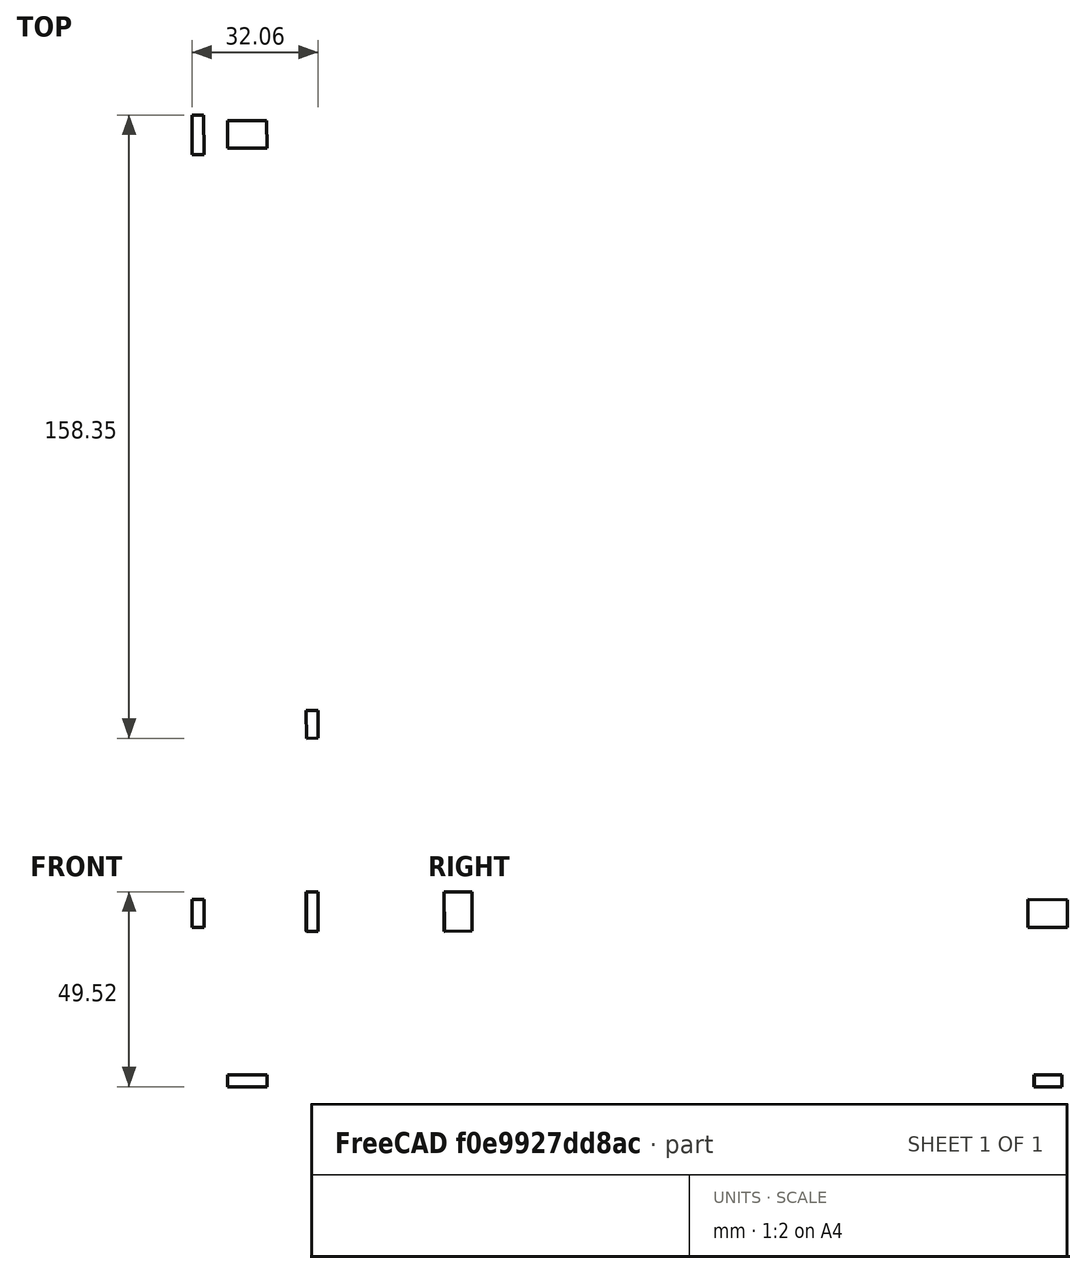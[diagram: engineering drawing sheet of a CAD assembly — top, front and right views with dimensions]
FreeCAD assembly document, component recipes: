
FREECAD ASSEMBLY — COMPONENT RECIPES ("3axis_robot_rotation")

This assembly document has 14 components, labeled P0..P13 below (a component is one placed body or linked part). 11 of them carry a construction recipe — the FreeCAD feature program that regenerates the part from scratch, quoted from this document or its linked companion documents; the rest are supplied as boundary geometry only. No exploded tour is included for this assembly.
COMPONENT P0 — recipe-attached ("arm0", a linked part whose construction recipe lives in a companion FreeCAD document of the same project; that document's serialized recipe follows).
Construction recipe (the companion document, serialized — sketch geometry with constraints, then the solid features built on it; lengths are millimeters unless a unit is written):

FCSTD DOCUMENT  (FreeCAD 2024.1R35694 (Git))
Label: arm0
License: All rights reserved
LicenseURL: https://en.wikipedia.org/wiki/All_rights_reserved
objects: Sketcher::SketchObject×11, PartDesign::Pad×6, PartDesign::Hole×3, PartDesign::Body×2, PartDesign::Pocket×2, PartDesign::Fillet×1, App::Part×1
note: 37 computed .brp shape members not serialized (recipe doc carries the construction recipe); baked Part::Feature solids carry a one-line shape summary decoded from their .brp

FEATURE [Sketcher::SketchObject] Sketch
  FullyConstrained = true
  MapMode = 5
  Support = -> [XY_Plane001]
  sketch-geometry (5):
    g0: Circle CenterX=0 CenterY=0 CenterZ=0 NormalX=0 NormalY=0 NormalZ=1 AngleXU=0 Radius=2.5
    g1: ArcOfCircle CenterX=0 CenterY=0 CenterZ=0 NormalX=0 NormalY=0 NormalZ=1 AngleXU=0 Radius=7.5 StartAngle=1.5708 EndAngle=4.71239
    g2: LineSegment StartX=-1.2e-15 StartY=7.5 StartZ=0 EndX=15 EndY=7.5 EndZ=0
    g3: LineSegment StartX=15 StartY=7.5 StartZ=0 EndX=15 EndY=-7.5 EndZ=0
    g4: LineSegment StartX=15 StartY=-7.5 StartZ=0 EndX=1.8e-15 EndY=-7.5 EndZ=0
  constraints (12):
    c: Coincident(g0,g-1)
    c: Coincident(g1,g0)
    c: Diameter(g0) = 5
    c: Diameter(g1) = 15
    c: Horizontal(g2)
    c: Coincident(g2,g3)
    c: Vertical(g3)
    c: Coincident(g3,g4)
    c: Horizontal(g4)
    c: Tangent(g1,g4) = 1.5708
    c: Tangent(g1,g2) = 1.5708
    c: DistanceX(g2,g2) = 15
FEATURE [PartDesign::Pad] Pad
  Direction = (0,0,1)
  Length = 20
  Length2 = 10
  Profile = -> Sketch
  ReferenceAxis = -> Sketch [N_Axis]
  Refine = true
  Type = 0
FEATURE [Sketcher::SketchObject] Sketch001
  ExternalGeometry = -> [Pad]
  FullyConstrained = true
  MapMode = 5
  Placement = pos=(15,0,0) rot=(0.57735,0.57735,0.57735;2.0944rad)
  Support = -> [Pad]
  sketch-geometry (8):
    g0: LineSegment StartX=-7.5 StartY=0 StartZ=0 EndX=-21 EndY=43 EndZ=0
    g1: LineSegment StartX=-21 StartY=43 StartZ=0 EndX=-21 EndY=85 EndZ=0
    g2: LineSegment StartX=-21 StartY=85 StartZ=0 EndX=21 EndY=85 EndZ=0
    g3: LineSegment StartX=21 StartY=85 StartZ=0 EndX=21 EndY=43 EndZ=0
    g4: LineSegment StartX=21 StartY=43 StartZ=0 EndX=7.5 EndY=0 EndZ=0
    g5: LineSegment StartX=7.5 StartY=0 StartZ=0 EndX=-7.5 EndY=0 EndZ=0
    g6: GeomPoint X=5.2e-15 Y=64 Z=0
    g7: Circle CenterX=5.2e-15 CenterY=64 CenterZ=0 NormalX=0 NormalY=0 NormalZ=1 AngleXU=0 Radius=11.25
  constraints (18):
    c: PointOnObject(g0,g-1)
    c: Coincident(g0,g1)
    c: Vertical(g1)
    c: Coincident(g1,g2)
    c: Coincident(g2,g3)
    c: Coincident(g3,g4)
    c: Coincident(g4,g5)
    c: Coincident(g5,g0)
    c: Symmetric(g0,g3,g-2)
    c: Symmetric(g1,g2,g-2)
    c: DistanceX(g2,g2) = 42
    c: DistanceY(g3,g3) = 42
    c: Symmetric(g0,g4,g-2)
    c: DistanceX(g5,g5) = 15
    c: Symmetric(g1,g3,g6)
    c: Coincident(g7,g6)
    c: Diameter(g7) = 22.5
    c: DistanceY(g-1,g3) = 43
FEATURE [PartDesign::Pad] Pad001
  BaseFeature = -> Pad
  Direction = (1,0,0)
  Length = 4
  Length2 = 10
  Profile = -> Sketch001
  ReferenceAxis = -> Sketch001 [N_Axis]
  Refine = true
  Reversed = true
  Type = 0
FEATURE [Sketcher::SketchObject] Sketch003
  ExternalGeometry = -> [Pad001]
  FullyConstrained = true
  MapMode = 5
  Placement = pos=(11,0,0) rot=(0.57735,-0.57735,-0.57735;2.0944rad)
  Support = -> [Pad001]
  sketch-geometry (5):
    g0: Circle CenterX=15.5 CenterY=79.5 CenterZ=0 NormalX=0 NormalY=0 NormalZ=1 AngleXU=0 Radius=1.5
    g1: LineSegment StartX=-5.2e-15 StartY=64 StartZ=0 EndX=11.25 EndY=64 EndZ=0
    g2: Circle CenterX=-15.5 CenterY=79.5 CenterZ=0 NormalX=0 NormalY=0 NormalZ=1 AngleXU=0 Radius=1.5
    g3: Circle CenterX=15.5 CenterY=48.5 CenterZ=0 NormalX=0 NormalY=0 NormalZ=1 AngleXU=0 Radius=1.5
    g4: Circle CenterX=-15.5 CenterY=48.5 CenterZ=0 NormalX=0 NormalY=0 NormalZ=1 AngleXU=0 Radius=1.5
  constraints (12):
    c: DistanceY(g-3,g0) = 15.5
    c: DistanceX(g-3,g0) = 15.5
    c: Diameter(g0) = 3
    c: Coincident(g1,g-3)
    c: Horizontal(g1)
    c: PointOnObject(g1,g-3)
    c: Diameter(g2) = 3
    c: Diameter(g3) = 3
    c: Diameter(g4) = 3
    c: Symmetric(g2,g0,g-2)
    c: Symmetric(g4,g3,g-2)
    c: Symmetric(g3,g0,g1)
FEATURE [PartDesign::Hole] Hole
  BaseFeature = -> Pad001
  CustomThreadClearance = 0
  Depth = 25
  DepthType = 0
  Diameter = 3.4
  DrillForDepth = false
  DrillPoint = 1
  DrillPointAngle = 118
  HoleCutCountersinkAngle = 90
  HoleCutCustomValues = false
  HoleCutDepth = 2
  HoleCutDiameter = 6.1
  HoleCutType = 1
  ModelThread = false
  Profile = -> Sketch003
  Refine = true
  Tapered = false
  TaperedAngle = 90
  ThreadClass = 0
  ThreadDepth = 25
  ThreadDepthType = 0
  ThreadDirection = 0
  ThreadFit = 0
  ThreadSize = 9
  ThreadType = 1
  Threaded = false
  UseCustomThreadClearance = false
FEATURE [Sketcher::SketchObject] Sketch004
  ExternalGeometry = -> [Hole]
  FullyConstrained = true
  MapMode = 5
  Placement = pos=(0,0,20) rot=(0,0,1;0rad)
  Support = -> [Hole]
  sketch-geometry (1):
    g0: Circle CenterX=0 CenterY=0 CenterZ=0 NormalX=0 NormalY=0 NormalZ=1 AngleXU=0 Radius=2.5
  constraints (2):
    c: Coincident(g0,g-3)
    c: Equal(g0,g-3)
FEATURE [PartDesign::Pad] Pad002
  BaseFeature = -> Hole
  Direction = (0,0,1)
  Length = 2
  Length2 = 10
  Profile = -> Sketch004
  ReferenceAxis = -> Sketch004 [N_Axis]
  Refine = true
  Reversed = true
  Type = 0
FEATURE [PartDesign::Body] Body  label="arm0-skel"
  Group = -> [Sketch,Pad,Sketch001,Pad001,Sketch003,Hole,Sketch004,Pad002]
  Origin = -> Origin001
  Tip = -> Pad002
FEATURE [Sketcher::SketchObject] Sketch008
  FullyConstrained = true
  MapMode = 5
  Support = -> [XY_Plane002]
  sketch-geometry (5):
    g0: Circle CenterX=0 CenterY=0 CenterZ=0 NormalX=0 NormalY=0 NormalZ=1 AngleXU=0 Radius=2.5
    g1: ArcOfCircle CenterX=0 CenterY=0 CenterZ=0 NormalX=0 NormalY=0 NormalZ=1 AngleXU=0 Radius=7.5 StartAngle=1.5708 EndAngle=4.71239
    g2: LineSegment StartX=-1.2e-15 StartY=7.5 StartZ=0 EndX=15 EndY=7.5 EndZ=0
    g3: LineSegment StartX=15 StartY=7.5 StartZ=0 EndX=15 EndY=-7.5 EndZ=0
    g4: LineSegment StartX=15 StartY=-7.5 StartZ=0 EndX=1.8e-15 EndY=-7.5 EndZ=0
  constraints (12):
    c: Coincident(g0,g-1)
    c: Coincident(g1,g0)
    c: Diameter(g0) = 5
    c: Diameter(g1) = 15
    c: Horizontal(g2)
    c: Coincident(g2,g3)
    c: Vertical(g3)
    c: Coincident(g3,g4)
    c: Horizontal(g4)
    c: Tangent(g1,g4) = 1.5708
    c: Tangent(g1,g2) = 1.5708
    c: DistanceX(g2,g2) = 15
FEATURE [PartDesign::Pad] Pad003
  Direction = (0,0,1)
  Length = 20
  Length2 = 10
  Profile = -> Sketch008
  ReferenceAxis = -> Sketch008 [N_Axis]
  Refine = true
  Type = 0
FEATURE [Sketcher::SketchObject] Sketch009
  ExternalGeometry = -> [Pad003]
  FullyConstrained = true
  MapMode = 5
  Placement = pos=(15,0,0) rot=(0.57735,0.57735,0.57735;2.0944rad)
  Support = -> [Pad003]
  sketch-geometry (8):
    g0: LineSegment StartX=-7.5 StartY=0 StartZ=0 EndX=-21 EndY=43 EndZ=0
    g1: LineSegment StartX=-21 StartY=43 StartZ=0 EndX=-21 EndY=85 EndZ=0
    g2: LineSegment StartX=-21 StartY=85 StartZ=0 EndX=21 EndY=85 EndZ=0
    g3: LineSegment StartX=21 StartY=85 StartZ=0 EndX=21 EndY=43 EndZ=0
    g4: LineSegment StartX=21 StartY=43 StartZ=0 EndX=7.5 EndY=0 EndZ=0
    g5: LineSegment StartX=7.5 StartY=0 StartZ=0 EndX=-7.5 EndY=0 EndZ=0
    g6: GeomPoint X=4.8e-15 Y=64 Z=0
    g7: Circle CenterX=4.8e-15 CenterY=64 CenterZ=0 NormalX=0 NormalY=0 NormalZ=1 AngleXU=0 Radius=11.25
  constraints (18):
    c: PointOnObject(g0,g-1)
    c: Coincident(g0,g1)
    c: Vertical(g1)
    c: Coincident(g1,g2)
    c: Coincident(g2,g3)
    c: Coincident(g3,g4)
    c: Coincident(g4,g5)
    c: Coincident(g5,g0)
    c: Symmetric(g0,g3,g-2)
    c: Symmetric(g1,g2,g-2)
    c: DistanceX(g2,g2) = 42
    c: DistanceY(g3,g3) = 42
    c: Symmetric(g0,g4,g-2)
    c: DistanceX(g5,g5) = 15
    c: Symmetric(g1,g3,g6)
    c: Coincident(g7,g6)
    c: Diameter(g7) = 22.5
    c: DistanceY(g-1,g3) = 43
FEATURE [PartDesign::Pad] Pad004
  BaseFeature = -> Pad003
  Direction = (1,0,0)
  Length = 4
  Length2 = 10
  Profile = -> Sketch009
  ReferenceAxis = -> Sketch009 [N_Axis]
  Refine = true
  Reversed = true
  Type = 0
FEATURE [Sketcher::SketchObject] Sketch010
  ExternalGeometry = -> [Pad004]
  FullyConstrained = true
  MapMode = 5
  Placement = pos=(11,0,0) rot=(0.57735,-0.57735,-0.57735;2.0944rad)
  Support = -> [Pad004]
  sketch-geometry (5):
    g0: Circle CenterX=15.5 CenterY=79.5 CenterZ=0 NormalX=0 NormalY=0 NormalZ=1 AngleXU=0 Radius=1.5
    g1: LineSegment StartX=-4.8e-15 StartY=64 StartZ=0 EndX=11.25 EndY=64 EndZ=0
    g2: Circle CenterX=-15.5 CenterY=79.5 CenterZ=0 NormalX=0 NormalY=0 NormalZ=1 AngleXU=0 Radius=1.5
    g3: Circle CenterX=15.5 CenterY=48.5 CenterZ=0 NormalX=0 NormalY=0 NormalZ=1 AngleXU=0 Radius=1.5
    g4: Circle CenterX=-15.5 CenterY=48.5 CenterZ=0 NormalX=0 NormalY=0 NormalZ=1 AngleXU=0 Radius=1.5
  constraints (12):
    c: DistanceY(g-3,g0) = 15.5
    c: DistanceX(g-3,g0) = 15.5
    c: Diameter(g0) = 3
    c: Coincident(g1,g-3)
    c: Horizontal(g1)
    c: PointOnObject(g1,g-3)
    c: Diameter(g2) = 3
    c: Diameter(g3) = 3
    c: Diameter(g4) = 3
    c: Symmetric(g2,g0,g-2)
    c: Symmetric(g4,g3,g-2)
    c: Symmetric(g3,g0,g1)
FEATURE [PartDesign::Hole] Hole002
  BaseFeature = -> Pad004
  CustomThreadClearance = 0
  Depth = 25
  DepthType = 0
  Diameter = 3.4
  DrillForDepth = false
  DrillPoint = 1
  DrillPointAngle = 118
  HoleCutCountersinkAngle = 90
  HoleCutCustomValues = false
  HoleCutDepth = 2
  HoleCutDiameter = 6.1
  HoleCutType = 1
  ModelThread = false
  Profile = -> Sketch010
  Refine = true
  Tapered = false
  TaperedAngle = 90
  ThreadClass = 0
  ThreadDepth = 25
  ThreadDepthType = 0
  ThreadDirection = 0
  ThreadFit = 0
  ThreadSize = 9
  ThreadType = 1
  Threaded = false
  UseCustomThreadClearance = false
FEATURE [Sketcher::SketchObject] Sketch011
  ExternalGeometry = -> [Hole002]
  FullyConstrained = true
  MapMode = 5
  Placement = pos=(0,0,20) rot=(0,0,1;0rad)
  Support = -> [Hole002]
  sketch-geometry (1):
    g0: Circle CenterX=0 CenterY=0 CenterZ=0 NormalX=0 NormalY=0 NormalZ=1 AngleXU=0 Radius=2.5
  constraints (2):
    c: Coincident(g0,g-3)
    c: Equal(g0,g-3)
FEATURE [PartDesign::Pad] Pad005
  BaseFeature = -> Hole002
  Direction = (0,0,1)
  Length = 2
  Length2 = 10
  Profile = -> Sketch011
  ReferenceAxis = -> Sketch011 [N_Axis]
  Refine = true
  Reversed = true
  Type = 0
FEATURE [Sketcher::SketchObject] Sketch012
  FullyConstrained = true
  MapMode = 5
  Placement = pos=(0,0,0) rot=(1,0,0;3.14159rad)
  Support = -> [Pad005]
  sketch-geometry (4):
    g0: LineSegment StartX=0 StartY=1 StartZ=0 EndX=0 EndY=-1 EndZ=0
    g1: LineSegment StartX=0 StartY=-1 StartZ=0 EndX=10 EndY=-1 EndZ=0
    g2: LineSegment StartX=10 StartY=-1 StartZ=0 EndX=10 EndY=1 EndZ=0
    g3: LineSegment StartX=10 StartY=1 StartZ=0 EndX=0 EndY=1 EndZ=0
  constraints (11):
    c: Coincident(g0,g1)
    c: Coincident(g1,g2)
    c: Coincident(g2,g3)
    c: Coincident(g3,g0)
    c: Vertical(g0)
    c: Horizontal(g1)
    c: Horizontal(g3)
    c: PointOnObject(g0,g-2)
    c: Symmetric(g1,g2,g-1)
    c: DistanceY(g2,g2) = 2
    c: DistanceX(g3,g3) = 10
FEATURE [PartDesign::Pocket] Pocket002
  BaseFeature = -> Pad005
  Direction = (0,0,1)
  Length = 5
  Length2 = 5
  Profile = -> Sketch012
  ReferenceAxis = -> Sketch012 [N_Axis]
  Refine = true
  Type = 1
FEATURE [Sketcher::SketchObject] Sketch013
  FullyConstrained = true
  MapMode = 5
  Placement = pos=(0,-7.5,0) rot=(1,0,0;1.5708rad)
  Support = -> [Pocket002]
  sketch-geometry (1):
    g0: Circle CenterX=6 CenterY=10 CenterZ=0 NormalX=0 NormalY=0 NormalZ=1 AngleXU=0 Radius=1.5
  constraints (3):
    c: DistanceY(g-1,g0) = 10
    c: DistanceX(g-1,g0) = 6
    c: Diameter(g0) = 3
FEATURE [PartDesign::Hole] Hole003
  BaseFeature = -> Pocket002
  CustomThreadClearance = 0
  Depth = 25
  DepthType = 0
  Diameter = 4.5
  DrillForDepth = false
  DrillPoint = 1
  DrillPointAngle = 118
  HoleCutCountersinkAngle = 90
  HoleCutCustomValues = false
  HoleCutDepth = 0
  HoleCutDiameter = 6.1
  HoleCutType = 0
  ModelThread = false
  Profile = -> Sketch013
  Refine = true
  Tapered = false
  TaperedAngle = 90
  ThreadClass = 0
  ThreadDepth = 25
  ThreadDepthType = 0
  ThreadDirection = 0
  ThreadFit = 0
  ThreadSize = 11
  ThreadType = 1
  Threaded = false
  UseCustomThreadClearance = false
FEATURE [Sketcher::SketchObject] Sketch014
  ExternalGeometry = -> [Hole003]
  FullyConstrained = true
  MapMode = 5
  Placement = pos=(0,7.5,0) rot=(0,0.707107,0.707107;3.14159rad)
  Support = -> [Hole003]
  sketch-geometry (7):
    g0: LineSegment StartX=-1.95855 StartY=10 StartZ=0 EndX=-3.97927 EndY=13.5 EndZ=0
    g1: LineSegment StartX=-3.97927 StartY=13.5 StartZ=0 EndX=-8.02073 EndY=13.5 EndZ=0
    g2: LineSegment StartX=-8.02073 StartY=13.5 StartZ=0 EndX=-10.0415 EndY=10 EndZ=0
    g3: LineSegment StartX=-10.0415 StartY=10 StartZ=0 EndX=-8.02073 EndY=6.5 EndZ=0
    g4: LineSegment StartX=-8.02073 StartY=6.5 StartZ=0 EndX=-3.97927 EndY=6.5 EndZ=0
    g5: LineSegment StartX=-3.97927 StartY=6.5 StartZ=0 EndX=-1.95855 EndY=10 EndZ=0
    g6: Circle CenterX=-6 CenterY=10 CenterZ=0 NormalX=0 NormalY=0 NormalZ=1 AngleXU=0 Radius=4.04145
  constraints (16):
    c: Coincident(g0,g1)
    c: Coincident(g1,g2)
    c: Coincident(g2,g3)
    c: Coincident(g3,g4)
    c: Coincident(g4,g5)
    c: Coincident(g5,g0)
    c: Equal(g0, g1-g5) x5
    c: PointOnObject(g0,g6)
    c: PointOnObject(g1,g6)
    c: PointOnObject(g2,g6)
    c: PointOnObject(g3,g6)
    c: PointOnObject(g4,g6)
    c: PointOnObject(g5,g6)
    c: Coincident(g6,g-3)
    c: Horizontal(g1)
    c: DistanceY(g4,g0) = 7
FEATURE [PartDesign::Pocket] Pocket003
  BaseFeature = -> Hole003
  Direction = (0,-1,2e-16)
  Length = 4
  Length2 = 5
  Profile = -> Sketch014
  ReferenceAxis = -> Sketch014 [N_Axis]
  Refine = true
  Type = 0
FEATURE [PartDesign::Fillet] Fillet
  Base = -> Pocket003 [Edge77,Edge78,Edge65,Edge54]
  BaseFeature = -> Pocket003
  Radius = 6
  Refine = true
  SupportTransform = false
  UseAllEdges = false
FEATURE [PartDesign::Body] Body001  label="arm0s"
  Group = -> [Sketch008,Pad003,Sketch009,Pad004,Sketch010,Hole002,Sketch011,Pad005,Sketch012,Pocket002,Sketch013,Hole003,Sketch014,Pocket003,Fillet]
  Origin = -> Origin002
  Tip = -> Fillet
FEATURE [App::Part] Part  label="arm0"
  Group = -> [Body,Body001]
  Origin = -> Origin
COMPONENT P1 — recipe-attached ("arm1", a linked part whose construction recipe lives in a companion FreeCAD document of the same project; that document's serialized recipe follows).
Construction recipe (the companion document, serialized — sketch geometry with constraints, then the solid features built on it; lengths are millimeters unless a unit is written):

FCSTD DOCUMENT  (FreeCAD 2024.1R35694 (Git))
Label: arm1
License: All rights reserved
LicenseURL: https://en.wikipedia.org/wiki/All_rights_reserved
objects: Sketcher::SketchObject×17, PartDesign::Pad×11, PartDesign::Chamfer×8, PartDesign::Plane×4, PartDesign::Hole×3, PartDesign::Pocket×3, PartDesign::Body×2, PartDesign::Fillet×1, App::Part×1
note: 75 computed .brp shape members not serialized (recipe doc carries the construction recipe); baked Part::Feature solids carry a one-line shape summary decoded from their .brp

FEATURE [Sketcher::SketchObject] Sketch
  FullyConstrained = true
  MapMode = 5
  Support = -> [XY_Plane001]
  sketch-geometry (5):
    g0: Circle CenterX=0 CenterY=0 CenterZ=0 NormalX=0 NormalY=0 NormalZ=1 AngleXU=0 Radius=2.5
    g1: ArcOfCircle CenterX=0 CenterY=0 CenterZ=0 NormalX=0 NormalY=0 NormalZ=1 AngleXU=0 Radius=7.5 StartAngle=1.5708 EndAngle=4.71239
    g2: LineSegment StartX=-1.2e-15 StartY=7.5 StartZ=0 EndX=15 EndY=7.5 EndZ=0
    g3: LineSegment StartX=15 StartY=7.5 StartZ=0 EndX=15 EndY=-7.5 EndZ=0
    g4: LineSegment StartX=15 StartY=-7.5 StartZ=0 EndX=1.8e-15 EndY=-7.5 EndZ=0
  constraints (12):
    c: Coincident(g0,g-1)
    c: Coincident(g1,g0)
    c: Diameter(g0) = 5
    c: Diameter(g1) = 15
    c: Horizontal(g2)
    c: Coincident(g2,g3)
    c: Vertical(g3)
    c: Coincident(g3,g4)
    c: Horizontal(g4)
    c: Tangent(g1,g4) = 1.5708
    c: Tangent(g1,g2) = 1.5708
    c: DistanceX(g2,g2) = 15
FEATURE [PartDesign::Pad] Pad
  Direction = (0,0,1)
  Length = 20
  Length2 = 10
  Profile = -> Sketch
  ReferenceAxis = -> Sketch [N_Axis]
  Refine = true
  Type = 0
FEATURE [Sketcher::SketchObject] Sketch001
  ExternalGeometry = -> [Pad]
  FullyConstrained = true
  MapMode = 5
  Placement = pos=(15,0,0) rot=(0.57735,0.57735,0.57735;2.0944rad)
  Support = -> [Pad]
  sketch-geometry (8):
    g0: LineSegment StartX=-7.5 StartY=0 StartZ=0 EndX=-21 EndY=11 EndZ=0
    g1: LineSegment StartX=-21 StartY=11 StartZ=0 EndX=-21 EndY=53 EndZ=0
    g2: LineSegment StartX=-21 StartY=53 StartZ=0 EndX=21 EndY=53 EndZ=0
    g3: LineSegment StartX=21 StartY=53 StartZ=0 EndX=21 EndY=11 EndZ=0
    g4: LineSegment StartX=21 StartY=11 StartZ=0 EndX=7.5 EndY=0 EndZ=0
    g5: LineSegment StartX=7.5 StartY=0 StartZ=0 EndX=-7.5 EndY=0 EndZ=0
    g6: GeomPoint X=-1.2e-15 Y=32 Z=0
    g7: Circle CenterX=-1.2e-15 CenterY=32 CenterZ=0 NormalX=0 NormalY=0 NormalZ=1 AngleXU=0 Radius=11.25
  constraints (18):
    c: PointOnObject(g0,g-1)
    c: Coincident(g0,g1)
    c: Vertical(g1)
    c: Coincident(g1,g2)
    c: Coincident(g2,g3)
    c: Coincident(g3,g4)
    c: Coincident(g4,g5)
    c: Coincident(g5,g0)
    c: Symmetric(g0,g3,g-2)
    c: Symmetric(g1,g2,g-2)
    c: DistanceX(g2,g2) = 42
    c: DistanceY(g3,g3) = 42
    c: Symmetric(g0,g4,g-2)
    c: DistanceX(g5,g5) = 15
    c: Symmetric(g1,g3,g6)
    c: Coincident(g7,g6)
    c: Diameter(g7) = 22.5
    c: DistanceY(g-1,g3) = 11
FEATURE [PartDesign::Pad] Pad001
  BaseFeature = -> Pad
  Direction = (1,0,0)
  Length = 4
  Length2 = 10
  Profile = -> Sketch001
  ReferenceAxis = -> Sketch001 [N_Axis]
  Refine = true
  Reversed = true
  Type = 0
FEATURE [Sketcher::SketchObject] Sketch003
  ExternalGeometry = -> [Pad001]
  FullyConstrained = true
  MapMode = 5
  Placement = pos=(11,0,0) rot=(0.57735,-0.57735,-0.57735;2.0944rad)
  Support = -> [Pad001]
  sketch-geometry (5):
    g0: Circle CenterX=15.5 CenterY=47.5 CenterZ=0 NormalX=0 NormalY=0 NormalZ=1 AngleXU=0 Radius=1.5
    g1: LineSegment StartX=1.2e-15 StartY=32 StartZ=0 EndX=11.25 EndY=32 EndZ=0
    g2: Circle CenterX=-15.5 CenterY=47.5 CenterZ=0 NormalX=0 NormalY=0 NormalZ=1 AngleXU=0 Radius=1.5
    g3: Circle CenterX=15.5 CenterY=16.5 CenterZ=0 NormalX=0 NormalY=0 NormalZ=1 AngleXU=0 Radius=1.5
    g4: Circle CenterX=-15.5 CenterY=16.5 CenterZ=0 NormalX=0 NormalY=0 NormalZ=1 AngleXU=0 Radius=1.5
  constraints (12):
    c: DistanceY(g-3,g0) = 15.5
    c: DistanceX(g-3,g0) = 15.5
    c: Diameter(g0) = 3
    c: Coincident(g1,g-3)
    c: Horizontal(g1)
    c: PointOnObject(g1,g-3)
    c: Diameter(g2) = 3
    c: Diameter(g3) = 3
    c: Diameter(g4) = 3
    c: Symmetric(g2,g0,g-2)
    c: Symmetric(g4,g3,g-2)
    c: Symmetric(g3,g0,g1)
FEATURE [PartDesign::Hole] Hole
  BaseFeature = -> Pad001
  CustomThreadClearance = 0
  Depth = 25
  DepthType = 0
  Diameter = 3.4
  DrillForDepth = false
  DrillPoint = 1
  DrillPointAngle = 118
  HoleCutCountersinkAngle = 90
  HoleCutCustomValues = false
  HoleCutDepth = 2
  HoleCutDiameter = 6.1
  HoleCutType = 1
  ModelThread = false
  Profile = -> Sketch003
  Refine = true
  Tapered = false
  TaperedAngle = 90
  ThreadClass = 0
  ThreadDepth = 25
  ThreadDepthType = 0
  ThreadDirection = 0
  ThreadFit = 0
  ThreadSize = 9
  ThreadType = 1
  Threaded = false
  UseCustomThreadClearance = false
FEATURE [Sketcher::SketchObject] Sketch004
  ExternalGeometry = -> [Hole]
  FullyConstrained = true
  MapMode = 5
  Placement = pos=(0,0,20) rot=(0,0,1;0rad)
  Support = -> [Hole]
  sketch-geometry (1):
    g0: Circle CenterX=0 CenterY=0 CenterZ=0 NormalX=0 NormalY=0 NormalZ=1 AngleXU=0 Radius=2.5
  constraints (2):
    c: Coincident(g0,g-3)
    c: Equal(g0,g-3)
FEATURE [PartDesign::Pad] Pad002
  BaseFeature = -> Hole
  Direction = (0,0,1)
  Length = 2
  Length2 = 10
  Profile = -> Sketch004
  ReferenceAxis = -> Sketch004 [N_Axis]
  Refine = true
  Reversed = true
  Type = 0
FEATURE [Sketcher::SketchObject] Sketch005
  FullyConstrained = true
  MapMode = 5
  Placement = pos=(0,0,0) rot=(1,0,0;3.14159rad)
  Support = -> [Pad002]
  sketch-geometry (4):
    g0: LineSegment StartX=0 StartY=1 StartZ=0 EndX=0 EndY=-1 EndZ=0
    g1: LineSegment StartX=0 StartY=-1 StartZ=0 EndX=10 EndY=-1 EndZ=0
    g2: LineSegment StartX=10 StartY=-1 StartZ=0 EndX=10 EndY=1 EndZ=0
    g3: LineSegment StartX=10 StartY=1 StartZ=0 EndX=0 EndY=1 EndZ=0
  constraints (11):
    c: Coincident(g0,g1)
    c: Coincident(g1,g2)
    c: Coincident(g2,g3)
    c: Coincident(g3,g0)
    c: Vertical(g0)
    c: Horizontal(g1)
    c: Horizontal(g3)
    c: PointOnObject(g0,g-2)
    c: Symmetric(g1,g2,g-1)
    c: DistanceY(g2,g2) = 2
    c: DistanceX(g3,g3) = 10
FEATURE [PartDesign::Pocket] Pocket
  BaseFeature = -> Pad002
  Direction = (0,0,1)
  Length = 5
  Length2 = 5
  Profile = -> Sketch005
  ReferenceAxis = -> Sketch005 [N_Axis]
  Refine = true
  Type = 1
FEATURE [Sketcher::SketchObject] Sketch006
  FullyConstrained = true
  MapMode = 5
  Placement = pos=(0,-7.5,0) rot=(1,0,0;1.5708rad)
  Support = -> [Pocket]
  sketch-geometry (1):
    g0: Circle CenterX=6 CenterY=10 CenterZ=0 NormalX=0 NormalY=0 NormalZ=1 AngleXU=0 Radius=1.5
  constraints (3):
    c: DistanceY(g-1,g0) = 10
    c: DistanceX(g-1,g0) = 6
    c: Diameter(g0) = 3
FEATURE [PartDesign::Hole] Hole001
  BaseFeature = -> Pocket
  CustomThreadClearance = 0
  Depth = 25
  DepthType = 0
  Diameter = 4.5
  DrillForDepth = false
  DrillPoint = 1
  DrillPointAngle = 118
  HoleCutCountersinkAngle = 90
  HoleCutCustomValues = false
  HoleCutDepth = 0
  HoleCutDiameter = 6.1
  HoleCutType = 0
  ModelThread = false
  Profile = -> Sketch006
  Refine = true
  Tapered = false
  TaperedAngle = 90
  ThreadClass = 0
  ThreadDepth = 25
  ThreadDepthType = 0
  ThreadDirection = 0
  ThreadFit = 0
  ThreadSize = 11
  ThreadType = 1
  Threaded = false
  UseCustomThreadClearance = false
FEATURE [Sketcher::SketchObject] Sketch007
  ExternalGeometry = -> [Hole001]
  FullyConstrained = true
  MapMode = 5
  Placement = pos=(0,7.5,0) rot=(0,0.707107,0.707107;3.14159rad)
  Support = -> [Hole001]
  sketch-geometry (7):
    g0: LineSegment StartX=-6 StartY=14.0415 StartZ=0 EndX=-9.5 EndY=12.0207 EndZ=0
    g1: LineSegment StartX=-9.5 StartY=12.0207 StartZ=0 EndX=-9.5 EndY=7.97927 EndZ=0
    g2: LineSegment StartX=-9.5 StartY=7.97927 StartZ=0 EndX=-6 EndY=5.95855 EndZ=0
    g3: LineSegment StartX=-6 StartY=5.95855 StartZ=0 EndX=-2.5 EndY=7.97927 EndZ=0
    g4: LineSegment StartX=-2.5 StartY=7.97927 StartZ=0 EndX=-2.5 EndY=12.0207 EndZ=0
    g5: LineSegment StartX=-2.5 StartY=12.0207 StartZ=0 EndX=-6 EndY=14.0415 EndZ=0
    g6: Circle CenterX=-6 CenterY=10 CenterZ=0 NormalX=0 NormalY=0 NormalZ=1 AngleXU=0 Radius=4.04145
  constraints (16):
    c: Coincident(g0,g1)
    c: Coincident(g1,g2)
    c: Coincident(g2,g3)
    c: Coincident(g3,g4)
    c: Coincident(g4,g5)
    c: Coincident(g5,g0)
    c: Equal(g0, g1-g5) x5
    c: PointOnObject(g0,g6)
    c: PointOnObject(g1,g6)
    c: PointOnObject(g2,g6)
    c: PointOnObject(g3,g6)
    c: PointOnObject(g4,g6)
    c: PointOnObject(g5,g6)
    c: Coincident(g6,g-3)
    c: Vertical(g4)
    c: DistanceX(g0,g4) = 7
FEATURE [PartDesign::Pocket] Pocket001
  BaseFeature = -> Hole001
  Direction = (0,-1,2e-16)
  Length = 4
  Length2 = 5
  Profile = -> Sketch007
  ReferenceAxis = -> Sketch007 [N_Axis]
  Refine = true
  Type = 0
FEATURE [Sketcher::SketchObject] Sketch008
  ExternalGeometry = -> [Pocket001]
  FullyConstrained = true
  MapMode = 5
  Placement = pos=(0,0,0) rot=(1,0,0;3.14159rad)
  Support = -> [Pocket001]
  sketch-geometry (5):
    g0: Circle CenterX=-150 CenterY=2.37e-14 CenterZ=0 NormalX=0 NormalY=0 NormalZ=1 AngleXU=0 Radius=8
    g1: ArcOfCircle CenterX=-150 CenterY=2.37e-14 CenterZ=0 NormalX=0 NormalY=0 NormalZ=1 AngleXU=0 Radius=11 StartAngle=0.276227 EndAngle=6.00696
    g2: ArcOfCircle CenterX=0 CenterY=0 CenterZ=0 NormalX=0 NormalY=0 NormalZ=1 AngleXU=0 Radius=7.5 StartAngle=2.73008 EndAngle=3.55311
    g3: LineSegment StartX=-139.417 StartY=3 StartZ=0 EndX=-6.87386 EndY=3 EndZ=0
    g4: LineSegment StartX=-139.417 StartY=-3 StartZ=0 EndX=-6.87386 EndY=-3 EndZ=0
  constraints (14):
    c: Coincident(g1,g0)
    c: Equal(g2,g-3)
    c: Horizontal(g3)
    c: Horizontal(g4)
    c: Coincident(g1,g4)
    c: Coincident(g1,g3)
    c: Coincident(g2,g3)
    c: Coincident(g2,g4)
    c: Symmetric(g1,g1,g-1)
    c: Distance(g1,g1) = 6
    c: Diameter(g0) = 16
    c: Diameter(g1) = 22
    c: DistanceX(g0,g-1) = 150
    c: Coincident(g2,g-3)
FEATURE [PartDesign::Pad] Pad003
  BaseFeature = -> Pocket001
  Direction = (0,0,-1)
  Length = 10
  Length2 = 10
  Profile = -> Sketch008
  ReferenceAxis = -> Sketch008 [N_Axis]
  Refine = true
  Reversed = true
  Type = 0
FEATURE [PartDesign::Plane] DatumPlane
  AttachmentOffset = pos=(0,0,-145) rot=(0,0,1;0rad)
  Length = 60
  MapMode = 5
  Placement = pos=(-130,0,0) rot=(0.57735,0.57735,0.57735;2.0944rad)
  ResizeMode = 0
  Support = -> [Pad003]
  Width = 60
FEATURE [Sketcher::SketchObject] Sketch009
  ExternalGeometry = -> [Pad003]
  FullyConstrained = true
  MapMode = 5
  Placement = pos=(-130,0,0) rot=(0.57735,0.57735,0.57735;2.0944rad)
  Support = -> [DatumPlane]
  sketch-geometry (5):
    g0: Circle CenterX=-1.2e-15 CenterY=32 CenterZ=0 NormalX=0 NormalY=0 NormalZ=1 AngleXU=0 Radius=8
    g1: ArcOfCircle CenterX=-1.2e-15 CenterY=32 CenterZ=0 NormalX=0 NormalY=0 NormalZ=1 AngleXU=0 Radius=11 StartAngle=4.98862 EndAngle=10.7193
    g2: LineSegment StartX=3 StartY=10 StartZ=0 EndX=-3 EndY=10 EndZ=0
    g3: LineSegment StartX=-3 StartY=10 StartZ=0 EndX=-3 EndY=21.417 EndZ=0
    g4: LineSegment StartX=3 StartY=10 StartZ=0 EndX=3 EndY=21.417 EndZ=0
  constraints (12):
    c: Coincident(g0,g-6)
    c: Coincident(g1,g0)
    c: Diameter(g0) = 16
    c: Diameter(g1) = 22
    c: Coincident(g2,g-4)
    c: Coincident(g2,g-5)
    c: Coincident(g2,g3)
    c: Coincident(g2,g4)
    c: Vertical(g4)
    c: Vertical(g3)
    c: Coincident(g1,g3)
    c: Coincident(g1,g4)
FEATURE [PartDesign::Pad] Pad004
  BaseFeature = -> Pad003
  Direction = (1,0,0)
  Length = 5
  Length2 = 10
  Profile = -> Sketch009
  ReferenceAxis = -> Sketch009 [N_Axis]
  Refine = true
  Type = 0
FEATURE [Sketcher::SketchObject] Sketch010
  FullyConstrained = true
  MapMode = 5
  Support = -> [XY_Plane002]
  sketch-geometry (5):
    g0: Circle CenterX=0 CenterY=0 CenterZ=0 NormalX=0 NormalY=0 NormalZ=1 AngleXU=0 Radius=2.5
    g1: ArcOfCircle CenterX=0 CenterY=0 CenterZ=0 NormalX=0 NormalY=0 NormalZ=1 AngleXU=0 Radius=7.5 StartAngle=1.5708 EndAngle=4.71239
    g2: LineSegment StartX=-1.2e-15 StartY=7.5 StartZ=0 EndX=15 EndY=7.5 EndZ=0
    g3: LineSegment StartX=15 StartY=7.5 StartZ=0 EndX=15 EndY=-7.5 EndZ=0
    g4: LineSegment StartX=15 StartY=-7.5 StartZ=0 EndX=1.8e-15 EndY=-7.5 EndZ=0
  constraints (12):
    c: Coincident(g0,g-1)
    c: Coincident(g1,g0)
    c: Diameter(g0) = 5
    c: Diameter(g1) = 15
    c: Horizontal(g2)
    c: Coincident(g2,g3)
    c: Vertical(g3)
    c: Coincident(g3,g4)
    c: Horizontal(g4)
    c: Tangent(g1,g4) = 1.5708
    c: Tangent(g1,g2) = 1.5708
    c: DistanceX(g2,g2) = 15
FEATURE [PartDesign::Pad] Pad005
  Direction = (0,0,1)
  Length = 20
  Length2 = 10
  Profile = -> Sketch010
  ReferenceAxis = -> Sketch010 [N_Axis]
  Refine = true
  Type = 0
FEATURE [Sketcher::SketchObject] Sketch011
  ExternalGeometry = -> [Pad005]
  FullyConstrained = true
  MapMode = 5
  Placement = pos=(15,0,0) rot=(0.57735,0.57735,0.57735;2.0944rad)
  Support = -> [Pad005]
  sketch-geometry (8):
    g0: LineSegment StartX=-7.5 StartY=0 StartZ=0 EndX=-21 EndY=11 EndZ=0
    g1: LineSegment StartX=-21 StartY=11 StartZ=0 EndX=-21 EndY=53 EndZ=0
    g2: LineSegment StartX=-21 StartY=53 StartZ=0 EndX=21 EndY=53 EndZ=0
    g3: LineSegment StartX=21 StartY=53 StartZ=0 EndX=21 EndY=11 EndZ=0
    g4: LineSegment StartX=21 StartY=11 StartZ=0 EndX=7.5 EndY=0 EndZ=0
    g5: LineSegment StartX=7.5 StartY=0 StartZ=0 EndX=-7.5 EndY=0 EndZ=0
    g6: GeomPoint X=-1.2e-15 Y=32 Z=0
    g7: Circle CenterX=-1.2e-15 CenterY=32 CenterZ=0 NormalX=0 NormalY=0 NormalZ=1 AngleXU=0 Radius=11.25
  constraints (18):
    c: PointOnObject(g0,g-1)
    c: Coincident(g0,g1)
    c: Vertical(g1)
    c: Coincident(g1,g2)
    c: Coincident(g2,g3)
    c: Coincident(g3,g4)
    c: Coincident(g4,g5)
    c: Coincident(g5,g0)
    c: Symmetric(g0,g3,g-2)
    c: Symmetric(g1,g2,g-2)
    c: DistanceX(g2,g2) = 42
    c: DistanceY(g3,g3) = 42
    c: Symmetric(g0,g4,g-2)
    c: DistanceX(g5,g5) = 15
    c: Symmetric(g1,g3,g6)
    c: Coincident(g7,g6)
    c: Diameter(g7) = 22.5
    c: DistanceY(g-1,g3) = 11
FEATURE [PartDesign::Pad] Pad006
  BaseFeature = -> Pad005
  Direction = (1,0,0)
  Length = 4
  Length2 = 10
  Profile = -> Sketch011
  ReferenceAxis = -> Sketch011 [N_Axis]
  Refine = true
  Reversed = true
  Type = 0
FEATURE [Sketcher::SketchObject] Sketch012
  ExternalGeometry = -> [Pad006]
  FullyConstrained = true
  MapMode = 5
  Placement = pos=(11,0,0) rot=(0.57735,-0.57735,-0.57735;2.0944rad)
  Support = -> [Pad006]
  sketch-geometry (5):
    g0: Circle CenterX=15.5 CenterY=47.5 CenterZ=0 NormalX=0 NormalY=0 NormalZ=1 AngleXU=0 Radius=1.5
    g1: LineSegment StartX=1.2e-15 StartY=32 StartZ=0 EndX=11.25 EndY=32 EndZ=0
    g2: Circle CenterX=-15.5 CenterY=47.5 CenterZ=0 NormalX=0 NormalY=0 NormalZ=1 AngleXU=0 Radius=1.5
    g3: Circle CenterX=15.5 CenterY=16.5 CenterZ=0 NormalX=0 NormalY=0 NormalZ=1 AngleXU=0 Radius=1.5
    g4: Circle CenterX=-15.5 CenterY=16.5 CenterZ=0 NormalX=0 NormalY=0 NormalZ=1 AngleXU=0 Radius=1.5
  constraints (12):
    c: DistanceY(g-3,g0) = 15.5
    c: DistanceX(g-3,g0) = 15.5
    c: Diameter(g0) = 3
    c: Coincident(g1,g-3)
    c: Horizontal(g1)
    c: PointOnObject(g1,g-3)
    c: Diameter(g2) = 3
    c: Diameter(g3) = 3
    c: Diameter(g4) = 3
    c: Symmetric(g2,g0,g-2)
    c: Symmetric(g4,g3,g-2)
    c: Symmetric(g3,g0,g1)
FEATURE [PartDesign::Hole] Hole002
  BaseFeature = -> Pad006
  CustomThreadClearance = 0
  Depth = 25
  DepthType = 0
  Diameter = 3.4
  DrillForDepth = false
  DrillPoint = 1
  DrillPointAngle = 118
  HoleCutCountersinkAngle = 90
  HoleCutCustomValues = false
  HoleCutDepth = 2
  HoleCutDiameter = 6.1
  HoleCutType = 1
  ModelThread = false
  Profile = -> Sketch012
  Refine = true
  Tapered = false
  TaperedAngle = 90
  ThreadClass = 0
  ThreadDepth = 25
  ThreadDepthType = 0
  ThreadDirection = 0
  ThreadFit = 0
  ThreadSize = 9
  ThreadType = 1
  Threaded = false
  UseCustomThreadClearance = false
FEATURE [Sketcher::SketchObject] Sketch013
  ExternalGeometry = -> [Hole002]
  FullyConstrained = true
  MapMode = 5
  Placement = pos=(0,0,20) rot=(0,0,1;0rad)
  Support = -> [Hole002]
  sketch-geometry (1):
    g0: Circle CenterX=0 CenterY=0 CenterZ=0 NormalX=0 NormalY=0 NormalZ=1 AngleXU=0 Radius=2.5
  constraints (2):
    c: Coincident(g0,g-3)
    c: Equal(g0,g-3)
FEATURE [PartDesign::Pad] Pad007
  BaseFeature = -> Hole002
  Direction = (0,0,1)
  Length = 2
  Length2 = 10
  Profile = -> Sketch013
  ReferenceAxis = -> Sketch013 [N_Axis]
  Refine = true
  Reversed = true
  Type = 0
FEATURE [Sketcher::SketchObject] Sketch017
  ExternalGeometry = -> [Pad007]
  FullyConstrained = true
  MapMode = 5
  Placement = pos=(0,0,0) rot=(1,0,0;3.14159rad)
  sketch-geometry (5):
    g0: Circle CenterX=-150 CenterY=4.1e-15 CenterZ=0 NormalX=0 NormalY=0 NormalZ=1 AngleXU=0 Radius=8
    g1: ArcOfCircle CenterX=-150 CenterY=4.1e-15 CenterZ=0 NormalX=0 NormalY=0 NormalZ=1 AngleXU=0 Radius=11 StartAngle=0.276227 EndAngle=6.00696
    g2: ArcOfCircle CenterX=7.9e-15 CenterY=2e-14 CenterZ=0 NormalX=0 NormalY=0 NormalZ=1 AngleXU=0 Radius=7.5 StartAngle=2.73008 EndAngle=3.55311
    g3: LineSegment StartX=-139.417 StartY=3 StartZ=0 EndX=-6.87386 EndY=3 EndZ=0
    g4: LineSegment StartX=-139.417 StartY=-3 StartZ=0 EndX=-6.87386 EndY=-3 EndZ=0
  constraints (15):
    c: Coincident(g1,g0)
    c: Horizontal(g3)
    c: Horizontal(g4)
    c: Coincident(g1,g4)
    c: Coincident(g1,g3)
    c: Coincident(g2,g3)
    c: Coincident(g2,g4)
    c: Symmetric(g1,g1,g-1)
    c: Distance(g1,g1) = 6
    c: Diameter(g0) = 16
    c: Diameter(g1) = 22
    c: DistanceX(g0,g-1) = 150
    c: Equal(g2,g-3)
    c: PointOnObject(g2,g-3)
    c: Equal(g4,g3)
FEATURE [PartDesign::Pad] Pad008
  BaseFeature = -> Pad007
  Direction = (0,0,-1)
  Length = 10
  Length2 = 10
  Profile = -> Sketch017
  ReferenceAxis = -> Sketch017 [N_Axis]
  Refine = true
  Reversed = true
  Type = 0
FEATURE [PartDesign::Plane] DatumPlane001
  AttachmentOffset = pos=(0,0,-145) rot=(0,0,1;0rad)
  Length = 60
  MapMode = 5
  Placement = pos=(-130,0,0) rot=(0.57735,0.57735,0.57735;2.0944rad)
  ResizeMode = 0
  Support = -> [Pad008]
  Width = 60
FEATURE [Sketcher::SketchObject] Sketch018
  ExternalGeometry = -> [Pad008]
  FullyConstrained = true
  MapMode = 5
  Placement = pos=(-130,0,0) rot=(0.57735,0.57735,0.57735;2.0944rad)
  Support = -> [DatumPlane001]
  sketch-geometry (5):
    g0: Circle CenterX=-1.2e-15 CenterY=32 CenterZ=0 NormalX=0 NormalY=0 NormalZ=1 AngleXU=0 Radius=8
    g1: ArcOfCircle CenterX=-1.2e-15 CenterY=32 CenterZ=0 NormalX=0 NormalY=0 NormalZ=1 AngleXU=0 Radius=11 StartAngle=4.98862 EndAngle=10.7193
    g2: LineSegment StartX=-3 StartY=10 StartZ=0 EndX=-3 EndY=21.417 EndZ=0
    g3: LineSegment StartX=3 StartY=10 StartZ=0 EndX=3 EndY=21.417 EndZ=0
    g4: LineSegment StartX=-3 StartY=10 StartZ=0 EndX=3 EndY=10 EndZ=0
  constraints (12):
    c: Coincident(g0,g-3)
    c: Coincident(g1,g0)
    c: Diameter(g0) = 16
    c: Diameter(g1) = 22
    c: Vertical(g3)
    c: Vertical(g2)
    c: Coincident(g1,g2)
    c: Coincident(g1,g3)
    c: Symmetric(g2,g3,g-2)
    c: Coincident(g4,g2)
    c: Coincident(g4,g3)
    c: Coincident(g2,g-4)
FEATURE [PartDesign::Pad] Pad009
  BaseFeature = -> Pad008
  Direction = (1,0,0)
  Length = 5
  Length2 = 10
  Profile = -> Sketch018
  ReferenceAxis = -> Sketch018 [N_Axis]
  Refine = true
  Type = 0
FEATURE [PartDesign::Body] Body001  label="arm1-skel"
  Group = -> [Sketch010,Pad005,Sketch011,Pad006,Sketch012,Hole002,Sketch013,Pad007,Sketch017,Pad008,DatumPlane001,Sketch018,Pad009]
  Origin = -> Origin002
  Tip = -> Pad009
FEATURE [PartDesign::Chamfer] Chamfer
  Angle = 15
  Base = -> Pad004
  BaseFeature = -> Pad004
  ChamferType = 2
  FlipDirection = true
  Refine = true
  Size = 1
  Size2 = 1
  SupportTransform = false
  UseAllEdges = false
FEATURE [PartDesign::Chamfer] Chamfer001
  Angle = 15
  Base = -> Chamfer [Edge18]
  BaseFeature = -> Chamfer
  ChamferType = 2
  FlipDirection = true
  Refine = true
  Size = 5
  Size2 = 1
  SupportTransform = false
  UseAllEdges = false
FEATURE [PartDesign::Chamfer] Chamfer002
  Angle = 15
  Base = -> Chamfer001 [Edge99]
  BaseFeature = -> Chamfer001
  ChamferType = 2
  FlipDirection = false
  Refine = true
  Size = 1
  Size2 = 1
  SupportTransform = false
  UseAllEdges = false
FEATURE [PartDesign::Chamfer] Chamfer003
  Angle = 15
  Base = -> Chamfer002 [Edge39]
  BaseFeature = -> Chamfer002
  ChamferType = 2
  FlipDirection = true
  Refine = true
  Size = 3
  Size2 = 1
  SupportTransform = false
  UseAllEdges = false
FEATURE [PartDesign::Chamfer] Chamfer004
  Angle = 15
  Base = -> Chamfer003 [Edge79]
  BaseFeature = -> Chamfer003
  ChamferType = 2
  FlipDirection = false
  Refine = true
  Size = 1
  Size2 = 1
  SupportTransform = false
  UseAllEdges = false
FEATURE [PartDesign::Chamfer] Chamfer005
  Angle = 15
  Base = -> Chamfer004 [Edge35,Edge87]
  BaseFeature = -> Chamfer004
  ChamferType = 2
  FlipDirection = true
  Refine = true
  Size = 1
  Size2 = 1
  SupportTransform = false
  UseAllEdges = false
FEATURE [PartDesign::Chamfer] Chamfer006
  Angle = 45
  Base = -> Chamfer005 [Edge5,Edge29]
  BaseFeature = -> Chamfer005
  ChamferType = 0
  FlipDirection = false
  Refine = true
  Size = 7
  Size2 = 1
  SupportTransform = false
  UseAllEdges = false
FEATURE [PartDesign::Plane] DatumPlane002
  Length = 60
  MapMode = 5
  Placement = pos=(-125,0,0) rot=(0.57735,0.57735,0.57735;2.0944rad)
  ResizeMode = 0
  Support = -> [Chamfer006]
  Width = 60
FEATURE [Sketcher::SketchObject] Sketch019
  ExternalGeometry = -> [Chamfer006]
  FullyConstrained = true
  MapMode = 5
  Placement = pos=(-125,0,0) rot=(0.57735,0.57735,0.57735;2.0944rad)
  Support = -> [DatumPlane002]
  sketch-geometry (4):
    g0: ArcOfCircle CenterX=-1.2e-15 CenterY=32 CenterZ=0 NormalX=0 NormalY=0 NormalZ=1 AngleXU=0 Radius=11 StartAngle=3.39743 EndAngle=6.02735
    g1: LineSegment StartX=-10.642 StartY=29.2164 StartZ=0 EndX=-3 EndY=0 EndZ=0
    g2: LineSegment StartX=-3 StartY=0 StartZ=0 EndX=3 EndY=0 EndZ=0
    g3: LineSegment StartX=3 StartY=0 StartZ=0 EndX=10.642 EndY=29.2164 EndZ=0
  constraints (9):
    c: Coincident(g0,g-3)
    c: PointOnObject(g-3,g0)
    c: PointOnObject(g1,g-1)
    c: Coincident(g1,g2)
    c: Coincident(g2,g3)
    c: Tangent(g0,g1) = -1.5708
    c: Tangent(g0,g3) = -1.5708
    c: Distance(g2,g2) = 6
    c: Symmetric(g1,g2,g-2)
FEATURE [PartDesign::Pad] Pad010
  BaseFeature = -> Chamfer006
  Direction = (1,0,0)
  Length = 10
  Length2 = 10
  Profile = -> Sketch019
  ReferenceAxis = -> Sketch019 [N_Axis]
  Refine = true
  Reversed = true
  Type = 3
  UpToFace = -> Chamfer006 [Face1]
FEATURE [PartDesign::Plane] DatumPlane003
  Length = 60
  MapMode = 5
  Placement = pos=(15,0,0) rot=(0.57735,0.57735,0.57735;2.0944rad)
  ResizeMode = 0
  Support = -> [Pad010]
  Width = 60
FEATURE [Sketcher::SketchObject] Sketch020
  ExternalGeometry = -> [Pad010]
  FullyConstrained = true
  MapMode = 5
  Placement = pos=(15,0,0) rot=(0.57735,0.57735,0.57735;2.0944rad)
  Support = -> [DatumPlane003]
  sketch-geometry (4):
    g0: ArcOfCircle CenterX=0 CenterY=47 CenterZ=0 NormalX=0 NormalY=0 NormalZ=1 AngleXU=0 Radius=2 StartAngle=0.664501 EndAngle=2.47709
    g1: ArcOfCircle CenterX=-1.2e-15 CenterY=32 CenterZ=0 NormalX=0 NormalY=0 NormalZ=1 AngleXU=0 Radius=11.25 StartAngle=0.664501 EndAngle=2.47709
    g2: LineSegment StartX=-8.85627 StartY=38.9375 StartZ=0 EndX=-1.57445 EndY=48.2333 EndZ=0
    g3: LineSegment StartX=8.85627 StartY=38.9375 StartZ=0 EndX=1.57445 EndY=48.2333 EndZ=0
  constraints (11):
    c: PointOnObject(g0,g-2)
    c: Coincident(g1,g-3)
    c: PointOnObject(g1,g-3)
    c: Horizontal(g1,g1)
    c: Tangent(g2,g1) = 1.5708
    c: Coincident(g3,g1)
    c: Equal(g3,g2)
    c: Coincident(g0,g2)
    c: Tangent(g0,g3) = -1.5708
    c: DistanceY(g1,g0) = 15
    c: Radius(g0) = 2
FEATURE [PartDesign::Pocket] Pocket002
  BaseFeature = -> Pad010
  Direction = (-1,0,0)
  Length = 5
  Length2 = 5
  Profile = -> Sketch020
  ReferenceAxis = -> Sketch020 [N_Axis]
  Refine = true
  Type = 0
FEATURE [PartDesign::Chamfer] Chamfer007
  Angle = 45
  Base = -> Pocket002 [Edge18,Edge6]
  BaseFeature = -> Pocket002
  ChamferType = 0
  FlipDirection = false
  Refine = true
  Size = 2
  Size2 = 1
  SupportTransform = false
  UseAllEdges = false
FEATURE [PartDesign::Fillet] Fillet
  Base = -> Chamfer007 [Edge65,Edge142,Edge84,Edge143]
  BaseFeature = -> Chamfer007
  Radius = 6
  Refine = true
  SupportTransform = false
  UseAllEdges = false
FEATURE [PartDesign::Body] Body  label="arm1s"
  Group = -> [Sketch,Pad,Sketch001,Pad001,Sketch003,Hole,Sketch004,Pad002,Sketch005,Pocket,Sketch006,Hole001,Sketch007,Pocket001,Sketch008,Pad003,DatumPlane,Sketch009,Pad004,Chamfer,Chamfer001,Chamfer002,Chamfer003,Chamfer004,Chamfer005,Chamfer006,DatumPlane002,Sketch019,Pad010,DatumPlane003,Sketch020,Pocket002,Chamfer007,Fillet]
  Origin = -> Origin001
  Tip = -> Fillet
FEATURE [App::Part] Part  label="arm1"
  Group = -> [Body001,Body]
  Origin = -> Origin
COMPONENT P2 — recipe-attached ("arm2", a linked part whose construction recipe lives in a companion FreeCAD document of the same project; that document's serialized recipe follows).
Construction recipe (the companion document, serialized — sketch geometry with constraints, then the solid features built on it; lengths are millimeters unless a unit is written):

FCSTD DOCUMENT  (FreeCAD 2024.1R35694 (Git))
Label: arm2
License: All rights reserved
LicenseURL: https://en.wikipedia.org/wiki/All_rights_reserved
objects: Sketcher::SketchObject×3, PartDesign::Pad×2, PartDesign::Body×2, PartDesign::Chamfer×1, PartDesign::Pocket×1, App::Part×1
note: 13 computed .brp shape members not serialized (recipe doc carries the construction recipe); baked Part::Feature solids carry a one-line shape summary decoded from their .brp

FEATURE [Sketcher::SketchObject] Sketch
  FullyConstrained = true
  MapMode = 5
  Support = -> [XY_Plane001]
  sketch-geometry (9):
    g0: ArcOfCircle CenterX=0 CenterY=0 CenterZ=0 NormalX=0 NormalY=0 NormalZ=1 AngleXU=0 Radius=2.5 StartAngle=2.2143 EndAngle=4.06889
    g1: ArcOfCircle CenterX=0 CenterY=0 CenterZ=0 NormalX=0 NormalY=0 NormalZ=1 AngleXU=0 Radius=4 StartAngle=0.523599 EndAngle=5.75959
    g2: LineSegment StartX=3.4641 StartY=2 StartZ=0 EndX=118 EndY=2 EndZ=0
    g3: LineSegment StartX=118 StartY=2 StartZ=0 EndX=120 EndY=0 EndZ=0
    g4: LineSegment StartX=120 StartY=0 StartZ=0 EndX=118 EndY=-2 EndZ=0
    g5: LineSegment StartX=118 StartY=-2 StartZ=0 EndX=3.4641 EndY=-2 EndZ=0
    g6: LineSegment StartX=-1.5 StartY=2 StartZ=0 EndX=1.5 EndY=2 EndZ=0
    g7: LineSegment StartX=-1.5 StartY=-2 StartZ=0 EndX=1.5 EndY=-2 EndZ=0
    g8: ArcOfCircle CenterX=0 CenterY=0 CenterZ=0 NormalX=0 NormalY=0 NormalZ=1 AngleXU=0 Radius=2.5 StartAngle=5.35589 EndAngle=7.21048
  constraints (26):
    c: Coincident(g0,g-1)
    c: Coincident(g1,g0)
    c: Horizontal(g2)
    c: Coincident(g2,g3)
    c: PointOnObject(g3,g-1)
    c: Coincident(g3,g4)
    c: Coincident(g4,g5)
    c: Horizontal(g6)
    c: Horizontal(g7)
    c: Equal(g6,g7)
    c: Coincident(g0,g6)
    c: Equal(g0,g8)
    c: Coincident(g0,g7)
    c: Coincident(g8,g7)
    c: Coincident(g0,g8)
    c: Diameter(g8) = 5
    c: DistanceY(g7,g6) = 4
    c: Symmetric(g4,g2,g-1)
    c: Angle(g3,g4) = 1.5708
    c: Distance(g2,g4) = 4
    c: Coincident(g1,g5)
    c: Diameter(g1) = 8
    c: DistanceX(g-1,g3) = 120
    c: Coincident(g1,g2)
    c: Equal(g5,g2)
    c: Coincident(g6,g8)
FEATURE [PartDesign::Pad] Pad
  Direction = (0,0,1)
  Length = 5
  Length2 = 10
  Profile = -> Sketch
  ReferenceAxis = -> Sketch [N_Axis]
  Refine = true
  Type = 0
FEATURE [PartDesign::Body] Body  label="arm2-skel"
  Group = -> [Sketch,Pad]
  Origin = -> Origin001
  Tip = -> Pad
FEATURE [Sketcher::SketchObject] Sketch001
  FullyConstrained = true
  MapMode = 5
  Support = -> [XY_Plane002]
  sketch-geometry (9):
    g0: ArcOfCircle CenterX=0 CenterY=0 CenterZ=0 NormalX=0 NormalY=0 NormalZ=1 AngleXU=0 Radius=2.5 StartAngle=2.2143 EndAngle=4.06889
    g1: ArcOfCircle CenterX=0 CenterY=0 CenterZ=0 NormalX=0 NormalY=0 NormalZ=1 AngleXU=0 Radius=4 StartAngle=0.523599 EndAngle=5.75959
    g2: LineSegment StartX=3.4641 StartY=2 StartZ=0 EndX=118 EndY=2 EndZ=0
    g3: LineSegment StartX=118 StartY=2 StartZ=0 EndX=120 EndY=0 EndZ=0
    g4: LineSegment StartX=120 StartY=0 StartZ=0 EndX=118 EndY=-2 EndZ=0
    g5: LineSegment StartX=118 StartY=-2 StartZ=0 EndX=3.4641 EndY=-2 EndZ=0
    g6: LineSegment StartX=-1.5 StartY=2 StartZ=0 EndX=1.5 EndY=2 EndZ=0
    g7: LineSegment StartX=-1.5 StartY=-2 StartZ=0 EndX=1.5 EndY=-2 EndZ=0
    g8: ArcOfCircle CenterX=0 CenterY=0 CenterZ=0 NormalX=0 NormalY=0 NormalZ=1 AngleXU=0 Radius=2.5 StartAngle=5.35589 EndAngle=7.21048
  constraints (26):
    c: Coincident(g0,g-1)
    c: Coincident(g1,g0)
    c: Horizontal(g2)
    c: Coincident(g2,g3)
    c: PointOnObject(g3,g-1)
    c: Coincident(g3,g4)
    c: Coincident(g4,g5)
    c: Horizontal(g6)
    c: Horizontal(g7)
    c: Equal(g6,g7)
    c: Coincident(g0,g6)
    c: Equal(g0,g8)
    c: Coincident(g0,g7)
    c: Coincident(g8,g7)
    c: Coincident(g0,g8)
    c: Diameter(g8) = 5
    c: DistanceY(g7,g6) = 4
    c: Symmetric(g4,g2,g-1)
    c: Angle(g3,g4) = 1.5708
    c: Distance(g2,g4) = 4
    c: Coincident(g1,g5)
    c: Diameter(g1) = 8
    c: DistanceX(g-1,g3) = 120
    c: Coincident(g1,g2)
    c: Equal(g5,g2)
    c: Coincident(g6,g8)
FEATURE [PartDesign::Pad] Pad001
  Direction = (0,0,1)
  Length = 5
  Length2 = 10
  Profile = -> Sketch001
  ReferenceAxis = -> Sketch001 [N_Axis]
  Refine = true
  Type = 0
FEATURE [PartDesign::Chamfer] Chamfer
  Angle = 15
  Base = -> Pad001 [Edge24,Edge21,Edge18,Edge26,Edge25,Edge27,Edge19,Edge22]
  BaseFeature = -> Pad001
  ChamferType = 2
  FlipDirection = false
  Refine = true
  Size = 1
  Size2 = 1
  SupportTransform = false
  UseAllEdges = false
FEATURE [Sketcher::SketchObject] Sketch002
  ExternalGeometry = -> [Chamfer]
  FullyConstrained = true
  MapMode = 5
  Placement = pos=(0,0,5) rot=(0,0,1;0rad)
  Support = -> [Chamfer]
  sketch-geometry (4):
    g0: LineSegment StartX=3.4641 StartY=-2 StartZ=0 EndX=203.464 EndY=-2 EndZ=0
    g1: LineSegment StartX=203.464 StartY=-2 StartZ=0 EndX=203.464 EndY=2 EndZ=0
    g2: LineSegment StartX=203.464 StartY=2 StartZ=0 EndX=3.4641 EndY=2 EndZ=0
    g3: ArcOfCircle CenterX=0 CenterY=0 CenterZ=0 NormalX=0 NormalY=0 NormalZ=1 AngleXU=0 Radius=4 StartAngle=5.75959 EndAngle=6.80678
  constraints (11):
    c: Coincident(g0,g1)
    c: Coincident(g1,g2)
    c: Vertical(g1)
    c: Horizontal(g0)
    c: Horizontal(g2)
    c: Coincident(g3,g-3)
    c: Coincident(g2,g-3)
    c: Coincident(g0,g-3)
    c: DistanceX(g2,g2) = 200
    c: Coincident(g3,g2)
    c: PointOnObject(g3,g0)
FEATURE [PartDesign::Pocket] Pocket
  BaseFeature = -> Chamfer
  Direction = (0,0,-1)
  Length = 1
  Length2 = 5
  Profile = -> Sketch002
  ReferenceAxis = -> Sketch002 [N_Axis]
  Refine = true
  Type = 0
FEATURE [PartDesign::Body] Body001  label="arm2s"
  Group = -> [Sketch001,Pad001,Chamfer,Sketch002,Pocket]
  Origin = -> Origin002
  Tip = -> Pocket
FEATURE [App::Part] Part  label="arm2"
  Group = -> [Body,Body001]
  Origin = -> Origin
COMPONENT P3 — geometry summary ("b625"; no construction recipe available for this part):
  bounding box: 16.0 x 16.0 x 5.1 mm
  tessellated surface: 1,008 triangles
  volume: 907 mm^3 (69% of its bounding box)
  symmetry: revolution-symmetric about the x axis through its bounding-box center; 2-fold rotationally symmetric about the z axis; mirror-symmetric across its x mid-plane, y mid-plane, z mid-plane
COMPONENT P4 — geometry summary ("b625_2"; no construction recipe available for this part):
  bounding box: 16.0 x 16.0 x 5.1 mm
  tessellated surface: 1,008 triangles
  volume: 907 mm^3 (69% of its bounding box)
  symmetry: revolution-symmetric about the x axis through its bounding-box center; 2-fold rotationally symmetric about the z axis; mirror-symmetric across its x mid-plane, y mid-plane, z mid-plane
COMPONENT P5 — geometry summary ("b625_3"; no construction recipe available for this part):
  bounding box: 16.0 x 16.0 x 5.1 mm
  tessellated surface: 1,008 triangles
  volume: 907 mm^3 (69% of its bounding box)
  symmetry: 2-fold rotationally symmetric about the x axis; revolution-symmetric about the y axis through its bounding-box center; 2-fold rotationally symmetric about the z axis; mirror-symmetric across its y mid-plane, z mid-plane
COMPONENT P6 — recipe-attached ("base 🔒", a linked part whose construction recipe lives in a companion FreeCAD document of the same project; that document's serialized recipe follows).
Construction recipe (the companion document, serialized — sketch geometry with constraints, then the solid features built on it; lengths are millimeters unless a unit is written):

FCSTD DOCUMENT  (FreeCAD 2024.1R35694 (Git))
Label: base
License: All rights reserved
LicenseURL: https://en.wikipedia.org/wiki/All_rights_reserved
objects: Sketcher::SketchObject×6, PartDesign::Pocket×2, PartDesign::Pad×1, PartDesign::Plane×1, PartDesign::AdditiveLoft×1, PartDesign::Hole×1, PartDesign::PolarPattern×1, PartDesign::Body×1, App::Part×1
note: 19 computed .brp shape members not serialized (recipe doc carries the construction recipe); baked Part::Feature solids carry a one-line shape summary decoded from their .brp

FEATURE [Sketcher::SketchObject] Sketch
  FullyConstrained = true
  MapMode = 5
  Support = -> [XY_Plane001]
  sketch-geometry (4):
    g0: LineSegment StartX=-25 StartY=-25 StartZ=0 EndX=25 EndY=-25 EndZ=0
    g1: LineSegment StartX=25 StartY=-25 StartZ=0 EndX=25 EndY=25 EndZ=0
    g2: LineSegment StartX=25 StartY=25 StartZ=0 EndX=-25 EndY=25 EndZ=0
    g3: LineSegment StartX=-25 StartY=25 StartZ=0 EndX=-25 EndY=-25 EndZ=0
  constraints (11):
    c: Coincident(g0,g1)
    c: Coincident(g1,g2)
    c: Coincident(g2,g3)
    c: Coincident(g3,g0)
    c: Horizontal(g0)
    c: Horizontal(g2)
    c: Vertical(g1)
    c: Vertical(g3)
    c: Symmetric(g0,g1,g-1)
    c: Equal(g1,g2)
    c: DistanceY(g1,g1) = 50
FEATURE [PartDesign::Pad] Pad
  Direction = (0,0,1)
  Length = 4
  Length2 = 10
  Profile = -> Sketch
  ReferenceAxis = -> Sketch [N_Axis]
  Refine = true
  Type = 0
FEATURE [PartDesign::Plane] DatumPlane
  AttachmentOffset = pos=(0,0,-50) rot=(0,0,1;0rad)
  Length = 120
  MapMode = 5
  Placement = pos=(0,0,-50) rot=(0,0,1;0rad)
  ResizeMode = 0
  Support = -> [XY_Plane001]
  Width = 120
FEATURE [Sketcher::SketchObject] Sketch001
  ExternalGeometry = -> [Pad]
  FullyConstrained = true
  MapMode = 5
  Support = -> [XY_Plane001]
  sketch-geometry (10):
    g0: LineSegment StartX=-25 StartY=25 StartZ=0 EndX=-25 EndY=-25 EndZ=0
    g1: LineSegment StartX=-25 StartY=-25 StartZ=0 EndX=25 EndY=-25 EndZ=0
    g2: LineSegment StartX=25 StartY=-25 StartZ=0 EndX=25 EndY=25 EndZ=0
    g3: LineSegment StartX=25 StartY=25 StartZ=0 EndX=-25 EndY=25 EndZ=0
    g4: GeomPoint X=0 Y=0 Z=0
    g5: LineSegment StartX=-23 StartY=23 StartZ=0 EndX=-23 EndY=-23 EndZ=0
    g6: LineSegment StartX=-23 StartY=-23 StartZ=0 EndX=23 EndY=-23 EndZ=0
    g7: LineSegment StartX=23 StartY=-23 StartZ=0 EndX=23 EndY=23 EndZ=0
    g8: LineSegment StartX=23 StartY=23 StartZ=0 EndX=-23 EndY=23 EndZ=0
    g9: GeomPoint X=0 Y=0 Z=0
  constraints (23):
    c: Coincident(g0,g1)
    c: Coincident(g1,g2)
    c: Coincident(g2,g3)
    c: Coincident(g3,g0)
    c: Vertical(g0)
    c: Vertical(g2)
    c: Horizontal(g1)
    c: Horizontal(g3)
    c: Symmetric(g2,g0,g4)
    c: Coincident(g4,g-1)
    c: Coincident(g1,g-4)
    c: Coincident(g5,g6)
    c: Coincident(g6,g7)
    c: Coincident(g7,g8)
    c: Coincident(g8,g5)
    c: Vertical(g5)
    c: Vertical(g7)
    c: Horizontal(g6)
    c: Horizontal(g8)
    c: Symmetric(g7,g5,g9)
    c: Coincident(g9,g4)
    c: DistanceX(g7,g2) = 2
    c: DistanceY(g7,g2) = 2
FEATURE [Sketcher::SketchObject] Sketch002
  FullyConstrained = true
  MapMode = 5
  Placement = pos=(0,0,-50) rot=(0,0,1;0rad)
  Support = -> [DatumPlane]
  sketch-geometry (10):
    g0: LineSegment StartX=-50 StartY=-50 StartZ=0 EndX=50 EndY=-50 EndZ=0
    g1: LineSegment StartX=50 StartY=-50 StartZ=0 EndX=50 EndY=50 EndZ=0
    g2: LineSegment StartX=50 StartY=50 StartZ=0 EndX=-50 EndY=50 EndZ=0
    g3: LineSegment StartX=-50 StartY=50 StartZ=0 EndX=-50 EndY=-50 EndZ=0
    g4: GeomPoint X=0 Y=0 Z=0
    g5: LineSegment StartX=-48 StartY=-48 StartZ=0 EndX=48 EndY=-48 EndZ=0
    g6: LineSegment StartX=48 StartY=-48 StartZ=0 EndX=48 EndY=48 EndZ=0
    g7: LineSegment StartX=48 StartY=48 StartZ=0 EndX=-48 EndY=48 EndZ=0
    g8: LineSegment StartX=-48 StartY=48 StartZ=0 EndX=-48 EndY=-48 EndZ=0
    g9: GeomPoint X=0 Y=0 Z=0
  constraints (24):
    c: Coincident(g0,g1)
    c: Coincident(g1,g2)
    c: Coincident(g2,g3)
    c: Coincident(g3,g0)
    c: Horizontal(g0)
    c: Horizontal(g2)
    c: Vertical(g1)
    c: Vertical(g3)
    c: Symmetric(g2,g0,g4)
    c: Coincident(g4,g-1)
    c: Coincident(g5,g6)
    c: Coincident(g6,g7)
    c: Coincident(g7,g8)
    c: Coincident(g8,g5)
    c: Horizontal(g5)
    c: Horizontal(g7)
    c: Vertical(g6)
    c: Vertical(g8)
    c: Symmetric(g7,g5,g9)
    c: Coincident(g9,g4)
    c: Equal(g7,g6)
    c: Equal(g1,g2)
    c: DistanceX(g6,g1) = 2
    c: DistanceY(g1,g1) = 100
FEATURE [PartDesign::AdditiveLoft] AdditiveLoft
  BaseFeature = -> Pad
  Closed = false
  Profile = -> Sketch001
  Refine = true
  Ruled = false
  Sections = -> [Sketch002]
FEATURE [Sketcher::SketchObject] Sketch003
  FullyConstrained = true
  MapMode = 5
  Placement = pos=(0,0,4) rot=(0,0,1;0rad)
  sketch-geometry (1):
    g0: Circle CenterX=0 CenterY=0 CenterZ=0 NormalX=0 NormalY=0 NormalZ=1 AngleXU=0 Radius=11.25
  constraints (2):
    c: Coincident(g0,g-1)
    c: Diameter(g0) = 22.5
FEATURE [PartDesign::Pocket] Pocket
  BaseFeature = -> AdditiveLoft
  Direction = (0,0,-1)
  Length = 5
  Length2 = 5
  Profile = -> Sketch003
  ReferenceAxis = -> Sketch003 [N_Axis]
  Refine = true
  Type = 0
FEATURE [Sketcher::SketchObject] Sketch004
  FullyConstrained = true
  MapMode = 5
  Placement = pos=(0,0,4) rot=(0,0,1;0rad)
  Support = -> [Pocket]
  sketch-geometry (4):
    g0: Circle CenterX=15.5 CenterY=15.5 CenterZ=0 NormalX=0 NormalY=0 NormalZ=1 AngleXU=0 Radius=1.5
    g1: Circle CenterX=15.5 CenterY=-15.5 CenterZ=0 NormalX=0 NormalY=0 NormalZ=1 AngleXU=0 Radius=1.5
    g2: Circle CenterX=-15.5 CenterY=-15.5 CenterZ=0 NormalX=0 NormalY=0 NormalZ=1 AngleXU=0 Radius=1.5
    g3: Circle CenterX=-15.5 CenterY=15.5 CenterZ=0 NormalX=0 NormalY=0 NormalZ=1 AngleXU=0 Radius=1.5
  constraints (9):
    c: Symmetric(g3,g0,g-2)
    c: Symmetric(g2,g3,g-1)
    c: Symmetric(g2,g1,g-2)
    c: Equal(g0,g3)
    c: Equal(g2,g1)
    c: Equal(g2,g3)
    c: Diameter(g3) = 3
    c: DistanceX(g3,g0) = 31
    c: DistanceY(g2,g3) = 31
FEATURE [PartDesign::Hole] Hole
  BaseFeature = -> Pocket
  CustomThreadClearance = 0
  Depth = 253.234
  DepthType = 1
  Diameter = 3.4
  DrillForDepth = false
  DrillPoint = 1
  DrillPointAngle = 118
  HoleCutCountersinkAngle = 90
  HoleCutCustomValues = false
  HoleCutDepth = 2
  HoleCutDiameter = 6.1
  HoleCutType = 1
  ModelThread = false
  Profile = -> Sketch004
  Refine = true
  Tapered = false
  TaperedAngle = 90
  ThreadClass = 0
  ThreadDepth = 253.234
  ThreadDepthType = 0
  ThreadDirection = 0
  ThreadFit = 0
  ThreadSize = 9
  ThreadType = 1
  Threaded = false
  UseCustomThreadClearance = false
FEATURE [Sketcher::SketchObject] Sketch005
  ExternalGeometry = -> [Hole]
  FullyConstrained = true
  MapMode = 5
  Placement = pos=(0,0,0) rot=(1,0,0;1.5708rad)
  Support = -> [XZ_Plane001]
  sketch-geometry (6):
    g0: ArcOfCircle CenterX=0 CenterY=-40 CenterZ=0 NormalX=0 NormalY=0 NormalZ=1 AngleXU=0 Radius=5 StartAngle=3.54648 EndAngle=5.87829
    g1: ArcOfCircle CenterX=-15 CenterY=-5 CenterZ=0 NormalX=0 NormalY=0 NormalZ=1 AngleXU=0 Radius=5 StartAngle=1.5708 EndAngle=3.54648
    g2: ArcOfCircle CenterX=15 CenterY=-5 CenterZ=0 NormalX=0 NormalY=0 NormalZ=1 AngleXU=0 Radius=5 StartAngle=5.87829 EndAngle=7.85398
    g3: LineSegment StartX=-15 StartY=-5.77e-14 StartZ=0 EndX=15 EndY=-5.77e-14 EndZ=0
    g4: LineSegment StartX=19.5957 StartY=-6.9696 StartZ=0 EndX=4.59573 EndY=-41.9696 EndZ=0
    g5: LineSegment StartX=-4.59573 StartY=-41.9696 StartZ=0 EndX=-19.5957 EndY=-6.9696 EndZ=0
  constraints (14):
    c: PointOnObject(g0,g-2)
    c: Tangent(g1,g-3)
    c: Horizontal(g3)
    c: Tangent(g0,g4) = 1.5708
    c: Tangent(g0,g5) = 1.5708
    c: Tangent(g2,g4) = 1.5708
    c: Tangent(g1,g5) = 1.5708
    c: Tangent(g2,g3) = 1.5708
    c: Equal(g0,g2)
    c: Radius(g0) = 5
    c: DistanceY(g0,g-1) = 40
    c: DistanceX(g1,g2) = 30
    c: Tangent(g1,g3) = 1.5708
    c: Symmetric(g1,g2,g-2)
FEATURE [PartDesign::Pocket] Pocket001
  BaseFeature = -> Hole
  Direction = (0,1,-2e-16)
  Length = 5
  Length2 = 5
  Profile = -> Sketch005
  ReferenceAxis = -> Sketch005 [N_Axis]
  Refine = true
  Type = 1
FEATURE [PartDesign::PolarPattern] PolarPattern
  Angle = 360
  Axis = -> Z_Axis001
  BaseFeature = -> Pocket001
  Mode = 0
  Occurrences = 4
  Offset = 120
  Originals = -> [Pocket001]
  Refine = true
FEATURE [PartDesign::Body] Body  label="base-skel"
  Group = -> [Sketch,Pad,DatumPlane,Sketch001,Sketch002,AdditiveLoft,Sketch003,Pocket,Sketch004,Hole,Sketch005,Pocket001,PolarPattern]
  Origin = -> Origin001
  Tip = -> PolarPattern
FEATURE [App::Part] Part  label="base"
  Group = -> [Body]
  Origin = -> Origin
COMPONENT P7 — recipe-attached ("bevel_gear", a linked part whose construction recipe lives in a companion FreeCAD document of the same project; that document's serialized recipe follows).
Construction recipe (the companion document, serialized — sketch geometry with constraints, then the solid features built on it; lengths are millimeters unless a unit is written):

FCSTD DOCUMENT  (FreeCAD 0.22R35966 (Git))
Label: bevel_gear
License: All rights reserved
LicenseURL: https://en.wikipedia.org/wiki/All_rights_reserved
objects: Sketcher::SketchObject×3, Part::FeaturePython×1, PartDesign::FeatureBase×1, PartDesign::Pocket×1, PartDesign::Groove×1, PartDesign::Chamfer×1, PartDesign::CoordinateSystem×1, PartDesign::Body×1, App::Part×1
note: 13 computed .brp shape members not serialized (recipe doc carries the construction recipe); baked Part::Feature solids carry a one-line shape summary decoded from their .brp

FEATURE [Part::FeaturePython] BevelGear  # WARN: FeaturePython — macro-defined, semantics opaque (R4)
  AttacherType = Attacher::AttachEngine3D
  angular_backlash = 0
  backlash = 0
  beta = 0
  clearance = 0.1
  dw = 36
  height = 7
  module = 2
  numpoints = 20
  pitch_angle = 45
  pressure_angle = 20
  reset_origin = true
  teeth = 18
  version = 1.2.0
  expr: angular_backlash = backlash / dw * 360 ° / pi
  expr: dw = teeth * module
FEATURE [PartDesign::FeatureBase] BaseFeature
  BaseFeature = -> BevelGear
  Suppressed = false
FEATURE [Sketcher::SketchObject] Sketch001
  FullyConstrained = true
  MapMode = 5
  Support = -> [XY_Plane001]
  sketch-geometry (4):
    g0: ArcOfCircle CenterX=0 CenterY=0 CenterZ=0 NormalX=0 NormalY=0 NormalZ=1 AngleXU=0 Radius=2.5 StartAngle=5.35589 EndAngle=7.21048
    g1: LineSegment StartX=-1.5 StartY=2 StartZ=0 EndX=1.5 EndY=2 EndZ=0
    g2: LineSegment StartX=-1.5 StartY=-2 StartZ=0 EndX=1.5 EndY=-2 EndZ=0
    g3: ArcOfCircle CenterX=0 CenterY=0 CenterZ=0 NormalX=0 NormalY=0 NormalZ=1 AngleXU=0 Radius=2.5 StartAngle=2.2143 EndAngle=4.06889
  constraints (12):
    c: Coincident(g0,g-1)
    c: Horizontal(g1)
    c: Horizontal(g2)
    c: Equal(g1,g2)
    c: Coincident(g3,g2)
    c: Coincident(g0,g2)
    c: Equal(g0,g3)
    c: Coincident(g0,g1)
    c: Coincident(g3,g1)
    c: Coincident(g0,g3)
    c: Diameter(g0) = 5
    c: Distance(g0,g2) = 4
FEATURE [PartDesign::Pocket] Pocket
  BaseFeature = -> BaseFeature
  Direction = (0,0,-1)
  Length = 5
  Length2 = 5
  Midplane = true
  Profile = -> Sketch001
  ReferenceAxis = -> Sketch001 [N_Axis]
  Refine = true
  Suppressed = false
  Type = 1
FEATURE [Sketcher::SketchObject] Sketch
  FullyConstrained = true
  MapMode = 5
  Placement = pos=(0,0,0) rot=(0.57735,0.57735,0.57735;2.0944rad)
  Support = -> [YZ_Plane001]
  sketch-geometry (3):
    g0: LineSegment StartX=-18 StartY=0 StartZ=0 EndX=0 EndY=18 EndZ=0
    g1: LineSegment StartX=0 StartY=18 StartZ=0 EndX=18 EndY=0 EndZ=0
    g2: LineSegment StartX=18 StartY=0 StartZ=0 EndX=-18 EndY=0 EndZ=0
  constraints (9):
    c: PointOnObject(g0,g-1)
    c: PointOnObject(g0,g-2)
    c: Coincident(g0,g1)
    c: PointOnObject(g1,g-1)
    c: Coincident(g1,g2)
    c: Coincident(g2,g0)
    c: Equal(g0,g1)
    c: DistanceX(g2,g2) = 36
    c: Angle(g0,g1) = 1.5708
FEATURE [Sketcher::SketchObject] Sketch002
  FullyConstrained = true
  MapMode = 5
  Placement = pos=(0,0,0) rot=(0.57735,0.57735,0.57735;2.0944rad)
  Support = -> [YZ_Plane001]
  sketch-geometry (3):
    g0: LineSegment StartX=13 StartY=0 StartZ=0 EndX=23 EndY=10 EndZ=0
    g1: LineSegment StartX=23 StartY=10 StartZ=0 EndX=23 EndY=0 EndZ=0
    g2: LineSegment StartX=23 StartY=0 StartZ=0 EndX=13 EndY=0 EndZ=0
  constraints (9):
    c: PointOnObject(g0,g-1)
    c: Coincident(g0,g1)
    c: PointOnObject(g1,g-1)
    c: Coincident(g1,g2)
    c: Coincident(g2,g0)
    c: DistanceX(g-1,g0) = 13
    c: DistanceX(g2,g2) = 10
    c: Vertical(g1)
    c: Angle(g2,g0) = 0.785398
FEATURE [PartDesign::Groove] Groove
  Angle = 360
  Angle2 = 60
  Axis = (0,0,1)
  Base = (0,0,0)
  BaseFeature = -> Pocket
  Profile = -> Sketch002
  ReferenceAxis = -> Sketch002 [V_Axis]
  Refine = true
  Suppressed = false
  Type = 0
FEATURE [PartDesign::Chamfer] Chamfer
  Angle = 15
  Base = -> Groove [Edge339,Edge337,Edge334,Edge335,Edge336,Edge338]
  BaseFeature = -> Groove
  ChamferType = 2
  FlipDirection = true
  Refine = true
  Size = 1
  Size2 = 1
  SupportTransform = false
  Suppressed = false
  UseAllEdges = false
FEATURE [PartDesign::CoordinateSystem] Local_CS
  AttacherType = Attacher::AttachEngine3D
  MapMode = 45
  Placement = pos=(5.50499e-08,-6.7455e-08,0) rot=(0,0,-1;1.2e-05rad)
  Support = -> [Chamfer]
FEATURE [PartDesign::Body] Body  label="gear"
  BaseFeature = -> BevelGear
  Group = -> [BaseFeature,Sketch001,Pocket,Sketch,Sketch002,Groove,Chamfer,Local_CS]
  Origin = -> Origin001
  Tip = -> Chamfer
FEATURE [App::Part] Part  label="bevel_gear"
  Group = -> [Body,BevelGear]
  Origin = -> Origin
COMPONENT P8 — same part as P7; its construction recipe is shown at P7.
COMPONENT P9 — recipe-attached ("nema17_48_1", a linked part whose construction recipe lives in a companion FreeCAD document of the same project; that document's serialized recipe follows).
Construction recipe (the companion document, serialized — sketch geometry with constraints, then the solid features built on it; lengths are millimeters unless a unit is written):

FCSTD DOCUMENT  (FreeCAD 2024.1R35694 (Git))
Label: nema17-48
License: All rights reserved
LicenseURL: http://en.wikipedia.org/wiki/All_rights_reserved
objects: Sketcher::SketchObject×4, PartDesign::Pad×3, PartDesign::Chamfer×2, PartDesign::Hole×1, PartDesign::Body×1, App::Part×1
note: 17 computed .brp shape members not serialized (recipe doc carries the construction recipe); baked Part::Feature solids carry a one-line shape summary decoded from their .brp

FEATURE [Sketcher::SketchObject] Sketch
  FullyConstrained = false
  MapMode = 5
  Support = -> [XY_Plane]
  sketch-geometry (5):
    g0: LineSegment StartX=21.15 StartY=21.15 StartZ=0 EndX=-21.15 EndY=21.15 EndZ=0
    g1: LineSegment StartX=-21.15 StartY=21.15 StartZ=0 EndX=-21.15 EndY=-21.15 EndZ=0
    g2: LineSegment StartX=-21.15 StartY=-21.15 StartZ=0 EndX=21.15 EndY=-21.15 EndZ=0
    g3: LineSegment StartX=21.15 StartY=-21.15 StartZ=0 EndX=21.15 EndY=21.15 EndZ=0
    g4: Circle CenterX=0 CenterY=0 CenterZ=0 NormalX=0 NormalY=0 NormalZ=1 AngleXU=0 Radius=29.9106
  constraints (14):
    c: Coincident(g0,g1)
    c: Coincident(g1,g2)
    c: Coincident(g2,g3)
    c: Coincident(g3,g0)
    c: Equal(g0,g1)
    c: Equal(g0,g2)
    c: Equal(g0,g3)
    c: PointOnObject(g0,g4)
    c: PointOnObject(g1,g4)
    c: PointOnObject(g2,g4)
    c: PointOnObject(g3,g4)
    c: Coincident(g4,g-1)
    c: Horizontal(g0)
    c: DistanceY(g3,g3) = 42.3
FEATURE [PartDesign::Pad] Pad
  Direction = (0,0,1)
  Length = 48
  Length2 = 100
  Profile = -> Sketch
  ReferenceAxis = -> Sketch [N_Axis]
  Type = 0
FEATURE [Sketcher::SketchObject] Sketch001
  FullyConstrained = true
  MapMode = 5
  Placement = pos=(0,0,48) rot=(0,0,1;0rad)
  Support = -> [Pad]
  sketch-geometry (1):
    g0: Circle CenterX=0 CenterY=0 CenterZ=0 NormalX=0 NormalY=0 NormalZ=1 AngleXU=0 Radius=11
  constraints (2):
    c: Coincident(g0,g-1)
    c: Diameter(g0) = 22
FEATURE [PartDesign::Pad] Pad001
  BaseFeature = -> Pad
  Direction = (0,0,1)
  Length = 2
  Length2 = 100
  Profile = -> Sketch001
  ReferenceAxis = -> Sketch001 [N_Axis]
  Type = 0
FEATURE [Sketcher::SketchObject] Sketch002
  FullyConstrained = true
  MapMode = 5
  Placement = pos=(0,0,48) rot=(0,0,1;0rad)
  Support = -> [Pad001]
  sketch-geometry (1):
    g0: Circle CenterX=0 CenterY=0 CenterZ=0 NormalX=0 NormalY=0 NormalZ=1 AngleXU=0 Radius=2.5
  constraints (2):
    c: Coincident(g0,g-1)
    c: Diameter(g0) = 5
FEATURE [PartDesign::Pad] Pad002
  BaseFeature = -> Pad001
  Direction = (0,0,1)
  Length = 24
  Length2 = 100
  Profile = -> Sketch002
  ReferenceAxis = -> Sketch002 [N_Axis]
  Type = 0
FEATURE [PartDesign::Chamfer] Chamfer
  Angle = 45
  Base = -> Pad002 [Edge18]
  BaseFeature = -> Pad002
  ChamferType = 0
  FlipDirection = false
  Size = 0.5
  Size2 = 1
  SupportTransform = true
  UseAllEdges = false
FEATURE [Sketcher::SketchObject] Sketch004
  FullyConstrained = true
  MapMode = 5
  Placement = pos=(0,0,48) rot=(0,0,1;0rad)
  sketch-geometry (4):
    g0: Circle CenterX=15.5 CenterY=-15.5 CenterZ=0 NormalX=0 NormalY=0 NormalZ=1 AngleXU=0 Radius=1.25
    g1: Circle CenterX=15.5 CenterY=15.5 CenterZ=0 NormalX=0 NormalY=0 NormalZ=1 AngleXU=0 Radius=1.25
    g2: Circle CenterX=-15.5 CenterY=15.5 CenterZ=0 NormalX=0 NormalY=0 NormalZ=1 AngleXU=0 Radius=1.25
    g3: Circle CenterX=-15.5 CenterY=-15.5 CenterZ=0 NormalX=0 NormalY=0 NormalZ=1 AngleXU=0 Radius=1.25
  constraints (9):
    c: Diameter(g0) = 2.5
    c: Symmetric(g1,g0,g-1)
    c: Symmetric(g1,g2,g-2)
    c: Symmetric(g3,g2,g-1)
    c: Equal(g2,g1)
    c: Equal(g1,g3)
    c: Equal(g3,g0)
    c: DistanceX(g2,g1) = 31
    c: DistanceY(g0,g1) = 31
FEATURE [PartDesign::Hole] Hole
  BaseFeature = -> Chamfer
  CustomThreadClearance = 0
  Depth = 4
  DepthType = 0
  Diameter = 3.4
  DrillForDepth = false
  DrillPoint = 1
  DrillPointAngle = 118
  HoleCutCountersinkAngle = 90
  HoleCutCustomValues = false
  HoleCutDepth = 0
  HoleCutDiameter = 1.6
  HoleCutType = 0
  ModelThread = false
  Profile = -> Sketch004
  Tapered = false
  TaperedAngle = 90
  ThreadClass = 0
  ThreadDepth = 4
  ThreadDepthType = 0
  ThreadDirection = 0
  ThreadFit = 0
  ThreadSize = 9
  ThreadType = 1
  Threaded = false
  UseCustomThreadClearance = false
FEATURE [PartDesign::Chamfer] Chamfer001
  Angle = 45
  Base = -> Hole [Edge20,Edge17,Edge22,Edge18]
  BaseFeature = -> Hole
  ChamferType = 0
  FlipDirection = false
  Size = 5
  Size2 = 1
  SupportTransform = true
  UseAllEdges = false
FEATURE [PartDesign::Body] Body  label="nema17"
  Group = -> [Sketch,Pad,Sketch001,Pad001,Sketch002,Pad002,Chamfer,Sketch004,Hole,Chamfer001]
  Origin = -> Origin
  Placement = pos=(0,0,-50) rot=(0,0,1;0rad)
  Tip = -> Chamfer001
FEATURE [App::Part] Part  label="nema17-48"
  Group = -> [Body]
  Origin = -> Origin001
COMPONENT P10 — same part as P9; its construction recipe is shown at P9.
COMPONENT P11 — same part as P9; its construction recipe is shown at P9.
COMPONENT P12 — recipe-attached ("shaft0", a linked part whose construction recipe lives in a companion FreeCAD document of the same project; that document's serialized recipe follows).
Construction recipe (the companion document, serialized — sketch geometry with constraints, then the solid features built on it; lengths are millimeters unless a unit is written):

FCSTD DOCUMENT  (FreeCAD 2024.1R35694 (Git))
Label: shaft0
License: All rights reserved
LicenseURL: https://en.wikipedia.org/wiki/All_rights_reserved
objects: Sketcher::SketchObject×10, PartDesign::Pocket×5, PartDesign::Revolution×2, PartDesign::Body×2, PartDesign::Chamfer×2, PartDesign::Pad×1, PartDesign::Hole×1, PartDesign::Fillet×1, PartDesign::Groove×1, App::Part×1
note: 38 computed .brp shape members not serialized (recipe doc carries the construction recipe); baked Part::Feature solids carry a one-line shape summary decoded from their .brp

FEATURE [Sketcher::SketchObject] Sketch
  FullyConstrained = true
  MapMode = 5
  Support = -> [XY_Plane001]
  sketch-geometry (8):
    g0: LineSegment StartX=0 StartY=0 StartZ=0 EndX=0 EndY=2.5 EndZ=0
    g1: LineSegment StartX=0 StartY=2.5 StartZ=0 EndX=-119.804 EndY=2.5 EndZ=0
    g2: LineSegment StartX=-119.804 StartY=2.5 StartZ=0 EndX=-125 EndY=5.5 EndZ=0
    g3: LineSegment StartX=-125 StartY=5.5 StartZ=0 EndX=-145 EndY=5.5 EndZ=0
    g4: LineSegment StartX=-145 StartY=5.5 StartZ=0 EndX=-145 EndY=2.5 EndZ=0
    g5: LineSegment StartX=-145 StartY=2.5 StartZ=0 EndX=-130 EndY=2.5 EndZ=0
    g6: LineSegment StartX=-130 StartY=2.5 StartZ=0 EndX=-130 EndY=0 EndZ=0
    g7: LineSegment StartX=-130 StartY=0 StartZ=0 EndX=0 EndY=0 EndZ=0
  constraints (23):
    c: Coincident(g-1,g0)
    c: PointOnObject(g0,g-2)
    c: Coincident(g0,g1)
    c: Horizontal(g1)
    c: Coincident(g1,g2)
    c: Coincident(g2,g3)
    c: Horizontal(g3)
    c: Coincident(g3,g4)
    c: Vertical(g4)
    c: Coincident(g4,g5)
    c: Horizontal(g5)
    c: Coincident(g5,g6)
    c: PointOnObject(g6,g-1)
    c: Vertical(g6)
    c: Coincident(g6,g7)
    c: Coincident(g7,g0)
    c: DistanceY(g-1,g5) = 2.5
    c: DistanceY(g4,g4) = 3
    c: DistanceY(g-1,g0) = 2.5
    c: DistanceX(g3,g3) = 20
    c: DistanceX(g5,g5) = 15
    c: DistanceX(g4,g-1) = 145
    c: Angle(g2,g3) = 0.523599
FEATURE [PartDesign::Revolution] Revolution
  Angle = 360
  Angle2 = 60
  Axis = (1,0,0)
  Base = (0,0,0)
  Profile = -> Sketch
  ReferenceAxis = -> Sketch [H_Axis]
  Refine = true
  Type = 0
FEATURE [Sketcher::SketchObject] Sketch001
  FullyConstrained = true
  MapMode = 5
  Placement = pos=(0,0,0) rot=(0.57735,0.57735,0.57735;2.0944rad)
  Support = -> [Revolution]
  sketch-geometry (8):
    g0: LineSegment StartX=-7.5 StartY=2 StartZ=0 EndX=7.5 EndY=2 EndZ=0
    g1: LineSegment StartX=7.5 StartY=2 StartZ=0 EndX=7.5 EndY=7 EndZ=0
    g2: LineSegment StartX=7.5 StartY=7 StartZ=0 EndX=-7.5 EndY=7 EndZ=0
    g3: LineSegment StartX=-7.5 StartY=7 StartZ=0 EndX=-7.5 EndY=2 EndZ=0
    g4: LineSegment StartX=-7.5 StartY=-7 StartZ=0 EndX=7.5 EndY=-7 EndZ=0
    g5: LineSegment StartX=7.5 StartY=-7 StartZ=0 EndX=7.5 EndY=-2 EndZ=0
    g6: LineSegment StartX=7.5 StartY=-2 StartZ=0 EndX=-7.5 EndY=-2 EndZ=0
    g7: LineSegment StartX=-7.5 StartY=-2 StartZ=0 EndX=-7.5 EndY=-7 EndZ=0
  constraints (21):
    c: Coincident(g0,g1)
    c: Coincident(g1,g2)
    c: Coincident(g2,g3)
    c: Coincident(g3,g0)
    c: Horizontal(g0)
    c: Vertical(g1)
    c: Vertical(g3)
    c: Coincident(g4,g5)
    c: Coincident(g5,g6)
    c: Coincident(g6,g7)
    c: Coincident(g7,g4)
    c: Horizontal(g4)
    c: Vertical(g5)
    c: Vertical(g7)
    c: Symmetric(g5,g0,g-1)
    c: Symmetric(g6,g0,g-1)
    c: Equal(g3,g7)
    c: Symmetric(g2,g1,g-2)
    c: DistanceY(g5,g0) = 4
    c: DistanceY(g5,g5) = 5
    c: DistanceX(g4,g4) = 15
FEATURE [PartDesign::Pocket] Pocket
  BaseFeature = -> Revolution
  Direction = (-1,0,0)
  Length = 7
  Length2 = 5
  Profile = -> Sketch001
  ReferenceAxis = -> Sketch001 [N_Axis]
  Refine = true
  Type = 0
FEATURE [PartDesign::Body] Body  label="shaft0_skel"
  Group = -> [Sketch,Revolution,Sketch001,Pocket]
  Origin = -> Origin001
  Tip = -> Pocket
FEATURE [Sketcher::SketchObject] Sketch002
  FullyConstrained = true
  MapMode = 5
  Support = -> [XY_Plane002]
  sketch-geometry (8):
    g0: LineSegment StartX=0 StartY=0 StartZ=0 EndX=0 EndY=2.5 EndZ=0
    g1: LineSegment StartX=0 StartY=2.5 StartZ=0 EndX=-119.631 EndY=2.5 EndZ=0
    g2: LineSegment StartX=-119.631 StartY=2.5 StartZ=0 EndX=-125 EndY=5.6 EndZ=0
    g3: LineSegment StartX=-125 StartY=5.6 StartZ=0 EndX=-145 EndY=5.6 EndZ=0
    g4: LineSegment StartX=-145 StartY=5.6 StartZ=0 EndX=-145 EndY=2.6 EndZ=0
    g5: LineSegment StartX=-145 StartY=2.6 StartZ=0 EndX=-130 EndY=2.6 EndZ=0
    g6: LineSegment StartX=-130 StartY=2.6 StartZ=0 EndX=-130 EndY=0 EndZ=0
    g7: LineSegment StartX=-130 StartY=0 StartZ=0 EndX=0 EndY=0 EndZ=0
  constraints (23):
    c: Coincident(g-1,g0)
    c: PointOnObject(g0,g-2)
    c: Coincident(g0,g1)
    c: Horizontal(g1)
    c: Coincident(g1,g2)
    c: Coincident(g2,g3)
    c: Horizontal(g3)
    c: Coincident(g3,g4)
    c: Vertical(g4)
    c: Coincident(g4,g5)
    c: Horizontal(g5)
    c: Coincident(g5,g6)
    c: PointOnObject(g6,g-1)
    c: Vertical(g6)
    c: Coincident(g6,g7)
    c: Coincident(g7,g0)
    c: DistanceY(g-1,g5) = 2.6
    c: DistanceY(g4,g4) = 3
    c: DistanceY(g-1,g0) = 2.5
    c: DistanceX(g3,g3) = 20
    c: DistanceX(g5,g5) = 15
    c: DistanceX(g4,g-1) = 145
    c: Angle(g2,g3) = 0.523599
FEATURE [PartDesign::Revolution] Revolution001
  Angle = 360
  Angle2 = 60
  Axis = (1,0,0)
  Base = (0,0,0)
  Profile = -> Sketch002
  ReferenceAxis = -> Sketch002 [H_Axis]
  Refine = true
  Type = 0
FEATURE [Sketcher::SketchObject] Sketch003
  FullyConstrained = true
  MapMode = 5
  Placement = pos=(0,0,0) rot=(0.57735,0.57735,0.57735;2.0944rad)
  Support = -> [Revolution001]
  sketch-geometry (8):
    g0: LineSegment StartX=-7.5 StartY=1.9 StartZ=0 EndX=7.5 EndY=1.9 EndZ=0
    g1: LineSegment StartX=7.5 StartY=1.9 StartZ=0 EndX=7.5 EndY=6.9 EndZ=0
    g2: LineSegment StartX=7.5 StartY=6.9 StartZ=0 EndX=-7.5 EndY=6.9 EndZ=0
    g3: LineSegment StartX=-7.5 StartY=6.9 StartZ=0 EndX=-7.5 EndY=1.9 EndZ=0
    g4: LineSegment StartX=-7.5 StartY=-6.9 StartZ=0 EndX=7.5 EndY=-6.9 EndZ=0
    g5: LineSegment StartX=7.5 StartY=-6.9 StartZ=0 EndX=7.5 EndY=-1.9 EndZ=0
    g6: LineSegment StartX=7.5 StartY=-1.9 StartZ=0 EndX=-7.5 EndY=-1.9 EndZ=0
    g7: LineSegment StartX=-7.5 StartY=-1.9 StartZ=0 EndX=-7.5 EndY=-6.9 EndZ=0
  constraints (21):
    c: Coincident(g0,g1)
    c: Coincident(g1,g2)
    c: Coincident(g2,g3)
    c: Coincident(g3,g0)
    c: Horizontal(g0)
    c: Vertical(g1)
    c: Vertical(g3)
    c: Coincident(g4,g5)
    c: Coincident(g5,g6)
    c: Coincident(g6,g7)
    c: Coincident(g7,g4)
    c: Horizontal(g4)
    c: Vertical(g5)
    c: Vertical(g7)
    c: Symmetric(g5,g0,g-1)
    c: Symmetric(g6,g0,g-1)
    c: Equal(g3,g7)
    c: Symmetric(g2,g1,g-2)
    c: DistanceY(g5,g0) = 3.8
    c: DistanceY(g5,g5) = 5
    c: DistanceX(g4,g4) = 15
FEATURE [PartDesign::Pocket] Pocket001
  BaseFeature = -> Revolution001
  Direction = (-1,0,0)
  Length = 7
  Length2 = 5
  Profile = -> Sketch003
  ReferenceAxis = -> Sketch003 [N_Axis]
  Refine = true
  Type = 0
FEATURE [PartDesign::Chamfer] Chamfer
  Angle = 15
  Base = -> Pocket001 [Edge20]
  BaseFeature = -> Pocket001
  ChamferType = 2
  FlipDirection = true
  Refine = true
  Size = 2
  Size2 = 1
  SupportTransform = false
  UseAllEdges = false
FEATURE [Sketcher::SketchObject] Sketch004
  ExternalGeometry = -> [Chamfer]
  FullyConstrained = true
  MapMode = 5
  Placement = pos=(-145,0,0) rot=(0.57735,-0.57735,-0.57735;2.0944rad)
  Support = -> [Chamfer]
  sketch-geometry (4):
    g0: ArcOfCircle CenterX=0 CenterY=0 CenterZ=0 NormalX=0 NormalY=0 NormalZ=1 AngleXU=0 Radius=5.6 StartAngle=0.189265 EndAngle=2.95233
    g1: LineSegment StartX=-5.5 StartY=1.05357 StartZ=0 EndX=-5.5 EndY=9 EndZ=0
    g2: LineSegment StartX=-5.5 StartY=9 StartZ=0 EndX=5.5 EndY=9 EndZ=0
    g3: LineSegment StartX=5.5 StartY=9 StartZ=0 EndX=5.5 EndY=1.05357 EndZ=0
  constraints (11):
    c: Coincident(g0,g-3)
    c: Vertical(g1)
    c: Coincident(g1,g2)
    c: Coincident(g2,g3)
    c: Vertical(g3)
    c: Symmetric(g1,g2,g-2)
    c: Coincident(g0,g1)
    c: Coincident(g0,g3)
    c: Equal(g0,g-3)
    c: DistanceX(g2,g2) = 11
    c: DistanceY(g-1,g2) = 9
FEATURE [PartDesign::Pad] Pad
  BaseFeature = -> Chamfer
  Direction = (-1,0,0)
  Length = 10
  Length2 = 10
  Profile = -> Sketch004
  ReferenceAxis = -> Sketch004 [N_Axis]
  Refine = true
  Reversed = true
  Type = 0
FEATURE [Sketcher::SketchObject] Sketch005
  ExternalGeometry = -> [Pad]
  FullyConstrained = true
  MapMode = 5
  Placement = pos=(0,-5.5,0) rot=(1,0,0;1.5708rad)
  Support = -> [Pad]
  sketch-geometry (1):
    g0: Circle CenterX=-140 CenterY=5 CenterZ=0 NormalX=0 NormalY=0 NormalZ=1 AngleXU=0 Radius=1.5
  constraints (3):
    c: DistanceX(g-3,g0) = 5
    c: DistanceY(g-1,g0) = 5
    c: Diameter(g0) = 3
FEATURE [PartDesign::Hole] Hole
  BaseFeature = -> Pad
  CustomThreadClearance = 0
  Depth = 25
  DepthType = 0
  Diameter = 3.4
  DrillForDepth = false
  DrillPoint = 1
  DrillPointAngle = 118
  HoleCutCountersinkAngle = 90
  HoleCutCustomValues = false
  HoleCutDepth = 2
  HoleCutDiameter = 6.1
  HoleCutType = 1
  ModelThread = false
  Profile = -> Sketch005
  Refine = true
  Tapered = false
  TaperedAngle = 90
  ThreadClass = 0
  ThreadDepth = 25
  ThreadDepthType = 0
  ThreadDirection = 0
  ThreadFit = 0
  ThreadSize = 9
  ThreadType = 1
  Threaded = false
  UseCustomThreadClearance = false
FEATURE [Sketcher::SketchObject] Sketch006
  ExternalGeometry = -> [Hole]
  FullyConstrained = true
  MapMode = 5
  Placement = pos=(0,5.5,0) rot=(0,0.707107,0.707107;3.14159rad)
  Support = -> [Hole]
  sketch-geometry (7):
    g0: LineSegment StartX=143.522 StartY=5 StartZ=0 EndX=141.761 EndY=8.05 EndZ=0
    g1: LineSegment StartX=141.761 StartY=8.05 StartZ=0 EndX=138.239 EndY=8.05 EndZ=0
    g2: LineSegment StartX=138.239 StartY=8.05 StartZ=0 EndX=136.478 EndY=5 EndZ=0
    g3: LineSegment StartX=136.478 StartY=5 StartZ=0 EndX=138.239 EndY=1.95 EndZ=0
    g4: LineSegment StartX=138.239 StartY=1.95 StartZ=0 EndX=141.761 EndY=1.95 EndZ=0
    g5: LineSegment StartX=141.761 StartY=1.95 StartZ=0 EndX=143.522 EndY=5 EndZ=0
    g6: Circle CenterX=140 CenterY=5 CenterZ=0 NormalX=0 NormalY=0 NormalZ=1 AngleXU=0 Radius=3.52184
  constraints (16):
    c: Coincident(g0,g1)
    c: Coincident(g1,g2)
    c: Coincident(g2,g3)
    c: Coincident(g3,g4)
    c: Coincident(g4,g5)
    c: Coincident(g5,g0)
    c: Equal(g0, g1-g5) x5
    c: PointOnObject(g0,g6)
    c: PointOnObject(g1,g6)
    c: PointOnObject(g2,g6)
    c: PointOnObject(g3,g6)
    c: PointOnObject(g4,g6)
    c: PointOnObject(g5,g6)
    c: Coincident(g6,g-3)
    c: DistanceY(g4,g0) = 6.1
    c: Horizontal(g4)
FEATURE [PartDesign::Pocket] Pocket002
  BaseFeature = -> Hole
  Direction = (0,-1,2e-16)
  Length = 3
  Length2 = 5
  Profile = -> Sketch006
  ReferenceAxis = -> Sketch006 [N_Axis]
  Refine = true
  Type = 0
FEATURE [Sketcher::SketchObject] Sketch007
  FullyConstrained = true
  MapMode = 5
  Placement = pos=(0,0,0) rot=(0.57735,0.57735,0.57735;2.0944rad)
  Support = -> [Pocket002]
  sketch-geometry (2):
    g0: Circle CenterX=0 CenterY=0 CenterZ=0 NormalX=0 NormalY=0 NormalZ=1 AngleXU=0 Radius=2.45
    g1: Circle CenterX=0 CenterY=0 CenterZ=0 NormalX=0 NormalY=0 NormalZ=1 AngleXU=0 Radius=5
  constraints (4):
    c: Coincident(g1,g0)
    c: Diameter(g0) = 4.9
    c: Diameter(g1) = 10
    c: Coincident(g0,g-1)
FEATURE [PartDesign::Pocket] Pocket003
  BaseFeature = -> Pocket002
  Direction = (-1,0,0)
  Length = 0
  Length2 = 5
  Profile = -> Sketch007
  ReferenceAxis = -> Sketch007 [N_Axis]
  Refine = true
  Type = 3
  UpToFace = -> Pocket002 [Face24]
FEATURE [PartDesign::Fillet] Fillet
  Base = -> Pocket003
  BaseFeature = -> Pocket003
  Radius = 3
  Refine = true
  SupportTransform = false
  UseAllEdges = false
FEATURE [Sketcher::SketchObject] Sketch008
  FullyConstrained = true
  MapMode = 5
  Placement = pos=(-145,0,0) rot=(0.57735,-0.57735,-0.57735;2.0944rad)
  Support = -> [Fillet]
  sketch-geometry (4):
    g0: LineSegment StartX=1 StartY=0 StartZ=0 EndX=1 EndY=15 EndZ=0
    g1: LineSegment StartX=1 StartY=15 StartZ=0 EndX=-1 EndY=15 EndZ=0
    g2: LineSegment StartX=-1 StartY=15 StartZ=0 EndX=-1 EndY=0 EndZ=0
    g3: LineSegment StartX=-1 StartY=0 StartZ=0 EndX=1 EndY=0 EndZ=0
  constraints (11):
    c: Coincident(g0,g1)
    c: Coincident(g1,g2)
    c: Coincident(g2,g3)
    c: Coincident(g3,g0)
    c: Vertical(g0)
    c: Vertical(g2)
    c: Horizontal(g3)
    c: PointOnObject(g0,g-1)
    c: Symmetric(g1,g0,g-2)
    c: DistanceX(g1,g1) = 2
    c: DistanceY(g0,g0) = 15
FEATURE [PartDesign::Pocket] Pocket004
  BaseFeature = -> Fillet
  Direction = (1,0,0)
  Length = 15
  Length2 = 5
  Profile = -> Sketch008
  ReferenceAxis = -> Sketch008 [N_Axis]
  Refine = true
  Type = 0
FEATURE [PartDesign::Chamfer] Chamfer001
  Angle = 45
  Base = -> Pocket004 [Edge86,Edge87,Edge85,Edge81,Edge84]
  BaseFeature = -> Pocket004
  ChamferType = 0
  FlipDirection = false
  Refine = true
  Size = 0.2
  Size2 = 1
  SupportTransform = false
  UseAllEdges = false
FEATURE [Sketcher::SketchObject] Sketch009
  ExternalGeometry = -> [Chamfer001]
  FullyConstrained = true
  MapMode = 5
  Support = -> [XY_Plane002]
  sketch-geometry (4):
    g0: LineSegment StartX=-7 StartY=3.3 StartZ=0 EndX=-7 EndY=2.3 EndZ=0
    g1: LineSegment StartX=-7 StartY=2.3 StartZ=0 EndX=-4 EndY=2.3 EndZ=0
    g2: LineSegment StartX=-4 StartY=2.3 StartZ=0 EndX=-4 EndY=3.3 EndZ=0
    g3: LineSegment StartX=-4 StartY=3.3 StartZ=0 EndX=-7 EndY=3.3 EndZ=0
  constraints (12):
    c: Coincident(g0,g1)
    c: Coincident(g1,g2)
    c: Coincident(g2,g3)
    c: Coincident(g3,g0)
    c: Vertical(g0)
    c: Vertical(g2)
    c: Horizontal(g1)
    c: Horizontal(g3)
    c: PointOnObject(g-3,g0)
    c: DistanceY(g-1,g1) = 2.3
    c: DistanceX(g3,g3) = 3
    c: DistanceY(g2,g2) = 1
FEATURE [PartDesign::Groove] Groove
  Angle = 360
  Angle2 = 60
  Axis = (1,0,0)
  Base = (0,0,0)
  BaseFeature = -> Chamfer001
  Profile = -> Sketch009
  ReferenceAxis = -> Sketch009 [H_Axis]
  Refine = true
  Reversed = true
  Type = 0
FEATURE [PartDesign::Body] Body001  label="shaft0s"
  Group = -> [Sketch002,Revolution001,Sketch003,Pocket001,Chamfer,Sketch004,Pad,Sketch005,Hole,Sketch006,Pocket002,Sketch007,Pocket003,Fillet,Sketch008,Pocket004,Chamfer001,Sketch009,Groove]
  Origin = -> Origin002
  Tip = -> Groove
FEATURE [App::Part] Part  label="shaft0"
  Group = -> [Body,Body001]
  Origin = -> Origin
COMPONENT P13 — recipe-attached ("shaft1", a linked part whose construction recipe lives in a companion FreeCAD document of the same project; that document's serialized recipe follows).
Construction recipe (the companion document, serialized — sketch geometry with constraints, then the solid features built on it; lengths are millimeters unless a unit is written):

FCSTD DOCUMENT  (FreeCAD 2024.1R35694 (Git))
Label: shaft1
License: All rights reserved
LicenseURL: https://en.wikipedia.org/wiki/All_rights_reserved
objects: Sketcher::SketchObject×7, PartDesign::Pocket×5, PartDesign::Revolution×2, PartDesign::Body×2, PartDesign::Chamfer×1, PartDesign::Plane×1, App::Part×1
note: 26 computed .brp shape members not serialized (recipe doc carries the construction recipe); baked Part::Feature solids carry a one-line shape summary decoded from their .brp

FEATURE [Sketcher::SketchObject] Sketch
  FullyConstrained = true
  MapMode = 5
  Support = -> [XY_Plane001]
  sketch-geometry (8):
    g0: LineSegment StartX=7 StartY=0 StartZ=0 EndX=7 EndY=2.5 EndZ=0
    g1: LineSegment StartX=7 StartY=2.5 StartZ=0 EndX=0 EndY=2.5 EndZ=0
    g2: LineSegment StartX=0 StartY=2.5 StartZ=0 EndX=0 EndY=3 EndZ=0
    g3: LineSegment StartX=0 StartY=3 StartZ=0 EndX=-4 EndY=3 EndZ=0
    g4: LineSegment StartX=-4 StartY=3 StartZ=0 EndX=-4 EndY=2.5 EndZ=0
    g5: LineSegment StartX=-4 StartY=2.5 StartZ=0 EndX=-19 EndY=2.5 EndZ=0
    g6: LineSegment StartX=-19 StartY=2.5 StartZ=0 EndX=-19 EndY=0 EndZ=0
    g7: LineSegment StartX=-19 StartY=0 StartZ=0 EndX=7 EndY=0 EndZ=0
  constraints (24):
    c: PointOnObject(g0,g-1)
    c: Vertical(g0)
    c: Coincident(g0,g1)
    c: PointOnObject(g1,g-2)
    c: Horizontal(g1)
    c: Coincident(g1,g2)
    c: PointOnObject(g2,g-2)
    c: Coincident(g2,g3)
    c: Horizontal(g3)
    c: Coincident(g3,g4)
    c: Coincident(g4,g5)
    c: Horizontal(g5)
    c: Coincident(g5,g6)
    c: PointOnObject(g6,g-1)
    c: Coincident(g6,g7)
    c: Coincident(g7,g0)
    c: Vertical(g6)
    c: Vertical(g4)
    c: DistanceY(g-1,g0) = 2.5
    c: DistanceY(g-1,g2) = 3
    c: DistanceY(g6,g6) = 2.5
    c: DistanceX(g1,g1) = 7
    c: DistanceX(g3,g3) = 4
    c: DistanceX(g5,g5) = 15
FEATURE [PartDesign::Revolution] Revolution
  Angle = 360
  Angle2 = 60
  Axis = (1,0,0)
  Base = (0,0,0)
  Profile = -> Sketch
  ReferenceAxis = -> Sketch [H_Axis]
  Refine = true
  Type = 0
FEATURE [Sketcher::SketchObject] Sketch001
  FullyConstrained = true
  MapMode = 5
  Placement = pos=(-19,0,0) rot=(0.57735,-0.57735,-0.57735;2.0944rad)
  Support = -> [Revolution]
  sketch-geometry (8):
    g0: LineSegment StartX=-5 StartY=7 StartZ=0 EndX=-5 EndY=2 EndZ=0
    g1: LineSegment StartX=-5 StartY=2 StartZ=0 EndX=5 EndY=2 EndZ=0
    g2: LineSegment StartX=5 StartY=2 StartZ=0 EndX=5 EndY=7 EndZ=0
    g3: LineSegment StartX=5 StartY=7 StartZ=0 EndX=-5 EndY=7 EndZ=0
    g4: LineSegment StartX=-5 StartY=-7 StartZ=0 EndX=5 EndY=-7 EndZ=0
    g5: LineSegment StartX=5 StartY=-7 StartZ=0 EndX=5 EndY=-2 EndZ=0
    g6: LineSegment StartX=5 StartY=-2 StartZ=0 EndX=-5 EndY=-2 EndZ=0
    g7: LineSegment StartX=-5 StartY=-2 StartZ=0 EndX=-5 EndY=-7 EndZ=0
  constraints (21):
    c: Coincident(g0,g1)
    c: Coincident(g1,g2)
    c: Coincident(g2,g3)
    c: Coincident(g3,g0)
    c: Vertical(g0)
    c: Vertical(g2)
    c: Horizontal(g3)
    c: Coincident(g4,g5)
    c: Coincident(g5,g6)
    c: Coincident(g6,g7)
    c: Coincident(g7,g4)
    c: Horizontal(g4)
    c: Vertical(g5)
    c: Vertical(g7)
    c: Symmetric(g1,g5,g-1)
    c: Symmetric(g0,g1,g-2)
    c: Symmetric(g6,g0,g-1)
    c: Equal(g2,g5)
    c: DistanceY(g5,g1) = 4
    c: DistanceY(g2,g2) = 5
    c: DistanceX(g3,g3) = 10
FEATURE [PartDesign::Pocket] Pocket
  BaseFeature = -> Revolution
  Direction = (1,0,0)
  Length = 5
  Length2 = 5
  Profile = -> Sketch001
  ReferenceAxis = -> Sketch001 [N_Axis]
  Refine = true
  Type = 0
FEATURE [Sketcher::SketchObject] Sketch002
  FullyConstrained = true
  MapMode = 5
  Placement = pos=(7,0,0) rot=(0.57735,0.57735,0.57735;2.0944rad)
  Support = -> [Pocket]
  sketch-geometry (8):
    g0: LineSegment StartX=-5 StartY=2 StartZ=0 EndX=5 EndY=2 EndZ=0
    g1: LineSegment StartX=5 StartY=2 StartZ=0 EndX=5 EndY=7 EndZ=0
    g2: LineSegment StartX=5 StartY=7 StartZ=0 EndX=-5 EndY=7 EndZ=0
    g3: LineSegment StartX=-5 StartY=7 StartZ=0 EndX=-5 EndY=2 EndZ=0
    g4: LineSegment StartX=-5 StartY=-7 StartZ=0 EndX=5 EndY=-7 EndZ=0
    g5: LineSegment StartX=5 StartY=-7 StartZ=0 EndX=5 EndY=-2 EndZ=0
    g6: LineSegment StartX=5 StartY=-2 StartZ=0 EndX=-5 EndY=-2 EndZ=0
    g7: LineSegment StartX=-5 StartY=-2 StartZ=0 EndX=-5 EndY=-7 EndZ=0
  constraints (21):
    c: Coincident(g0,g1)
    c: Coincident(g1,g2)
    c: Coincident(g2,g3)
    c: Coincident(g3,g0)
    c: Horizontal(g0)
    c: Vertical(g1)
    c: Vertical(g3)
    c: Coincident(g4,g5)
    c: Coincident(g5,g6)
    c: Coincident(g6,g7)
    c: Coincident(g7,g4)
    c: Horizontal(g4)
    c: Vertical(g5)
    c: Vertical(g7)
    c: Symmetric(g0,g6,g-1)
    c: Symmetric(g0,g5,g-1)
    c: Symmetric(g2,g1,g-2)
    c: Equal(g1,g5)
    c: DistanceY(g5,g0) = 4
    c: DistanceY(g1,g1) = 5
    c: DistanceX(g2,g2) = 10
FEATURE [PartDesign::Pocket] Pocket001
  BaseFeature = -> Pocket
  Direction = (-1,0,0)
  Length = 7
  Length2 = 5
  Profile = -> Sketch002
  ReferenceAxis = -> Sketch002 [N_Axis]
  Refine = true
  Type = 0
FEATURE [PartDesign::Body] Body  label="shaft1_skel"
  Group = -> [Sketch,Revolution,Sketch001,Pocket,Sketch002,Pocket001]
  Origin = -> Origin001
  Tip = -> Pocket001
FEATURE [Sketcher::SketchObject] Sketch003
  FullyConstrained = true
  MapMode = 5
  Support = -> [XY_Plane002]
  sketch-geometry (8):
    g0: LineSegment StartX=7 StartY=0 StartZ=0 EndX=7 EndY=2.45 EndZ=0
    g1: LineSegment StartX=7 StartY=2.45 StartZ=0 EndX=0 EndY=2.45 EndZ=0
    g2: LineSegment StartX=0 StartY=2.45 StartZ=0 EndX=0 EndY=3 EndZ=0
    g3: LineSegment StartX=0 StartY=3 StartZ=0 EndX=-4 EndY=3 EndZ=0
    g4: LineSegment StartX=-4 StartY=3 StartZ=0 EndX=-4 EndY=2.5 EndZ=0
    g5: LineSegment StartX=-4 StartY=2.5 StartZ=0 EndX=-19 EndY=2.5 EndZ=0
    g6: LineSegment StartX=-19 StartY=2.5 StartZ=0 EndX=-19 EndY=0 EndZ=0
    g7: LineSegment StartX=-19 StartY=0 StartZ=0 EndX=7 EndY=0 EndZ=0
  constraints (24):
    c: PointOnObject(g0,g-1)
    c: Vertical(g0)
    c: Coincident(g0,g1)
    c: PointOnObject(g1,g-2)
    c: Horizontal(g1)
    c: Coincident(g1,g2)
    c: PointOnObject(g2,g-2)
    c: Coincident(g2,g3)
    c: Horizontal(g3)
    c: Coincident(g3,g4)
    c: Coincident(g4,g5)
    c: Horizontal(g5)
    c: Coincident(g5,g6)
    c: PointOnObject(g6,g-1)
    c: Coincident(g6,g7)
    c: Coincident(g7,g0)
    c: Vertical(g6)
    c: Vertical(g4)
    c: DistanceY(g-1,g0) = 2.45
    c: DistanceY(g-1,g2) = 3
    c: DistanceY(g6,g6) = 2.5
    c: DistanceX(g1,g1) = 7
    c: DistanceX(g3,g3) = 4
    c: DistanceX(g5,g5) = 15
FEATURE [PartDesign::Revolution] Revolution001
  Angle = 360
  Angle2 = 60
  Axis = (1,0,0)
  Base = (0,0,0)
  Profile = -> Sketch003
  ReferenceAxis = -> Sketch003 [H_Axis]
  Refine = true
  Type = 0
FEATURE [Sketcher::SketchObject] Sketch004
  FullyConstrained = true
  MapMode = 5
  Placement = pos=(-19,0,0) rot=(0.57735,-0.57735,-0.57735;2.0944rad)
  Support = -> [Revolution001]
  sketch-geometry (8):
    g0: LineSegment StartX=-5 StartY=6.9 StartZ=0 EndX=-5 EndY=1.9 EndZ=0
    g1: LineSegment StartX=-5 StartY=1.9 StartZ=0 EndX=5 EndY=1.9 EndZ=0
    g2: LineSegment StartX=5 StartY=1.9 StartZ=0 EndX=5 EndY=6.9 EndZ=0
    g3: LineSegment StartX=5 StartY=6.9 StartZ=0 EndX=-5 EndY=6.9 EndZ=0
    g4: LineSegment StartX=-5 StartY=-6.9 StartZ=0 EndX=5 EndY=-6.9 EndZ=0
    g5: LineSegment StartX=5 StartY=-6.9 StartZ=0 EndX=5 EndY=-1.9 EndZ=0
    g6: LineSegment StartX=5 StartY=-1.9 StartZ=0 EndX=-5 EndY=-1.9 EndZ=0
    g7: LineSegment StartX=-5 StartY=-1.9 StartZ=0 EndX=-5 EndY=-6.9 EndZ=0
  constraints (21):
    c: Coincident(g0,g1)
    c: Coincident(g1,g2)
    c: Coincident(g2,g3)
    c: Coincident(g3,g0)
    c: Vertical(g0)
    c: Vertical(g2)
    c: Horizontal(g3)
    c: Coincident(g4,g5)
    c: Coincident(g5,g6)
    c: Coincident(g6,g7)
    c: Coincident(g7,g4)
    c: Horizontal(g4)
    c: Vertical(g5)
    c: Vertical(g7)
    c: Symmetric(g1,g5,g-1)
    c: Symmetric(g0,g1,g-2)
    c: Symmetric(g6,g0,g-1)
    c: Equal(g2,g5)
    c: DistanceY(g5,g1) = 3.8
    c: DistanceY(g2,g2) = 5
    c: DistanceX(g3,g3) = 10
FEATURE [PartDesign::Pocket] Pocket002
  BaseFeature = -> Revolution001
  Direction = (1,0,0)
  Length = 5
  Length2 = 5
  Profile = -> Sketch004
  ReferenceAxis = -> Sketch004 [N_Axis]
  Refine = true
  Type = 0
FEATURE [Sketcher::SketchObject] Sketch005
  FullyConstrained = true
  MapMode = 5
  Placement = pos=(7,0,0) rot=(0.57735,0.57735,0.57735;2.0944rad)
  Support = -> [Pocket002]
  sketch-geometry (8):
    g0: LineSegment StartX=-5 StartY=1.9 StartZ=0 EndX=5 EndY=1.9 EndZ=0
    g1: LineSegment StartX=5 StartY=1.9 StartZ=0 EndX=5 EndY=6.9 EndZ=0
    g2: LineSegment StartX=5 StartY=6.9 StartZ=0 EndX=-5 EndY=6.9 EndZ=0
    g3: LineSegment StartX=-5 StartY=6.9 StartZ=0 EndX=-5 EndY=1.9 EndZ=0
    g4: LineSegment StartX=-5 StartY=-6.9 StartZ=0 EndX=5 EndY=-6.9 EndZ=0
    g5: LineSegment StartX=5 StartY=-6.9 StartZ=0 EndX=5 EndY=-1.9 EndZ=0
    g6: LineSegment StartX=5 StartY=-1.9 StartZ=0 EndX=-5 EndY=-1.9 EndZ=0
    g7: LineSegment StartX=-5 StartY=-1.9 StartZ=0 EndX=-5 EndY=-6.9 EndZ=0
  constraints (21):
    c: Coincident(g0,g1)
    c: Coincident(g1,g2)
    c: Coincident(g2,g3)
    c: Coincident(g3,g0)
    c: Horizontal(g0)
    c: Vertical(g1)
    c: Vertical(g3)
    c: Coincident(g4,g5)
    c: Coincident(g5,g6)
    c: Coincident(g6,g7)
    c: Coincident(g7,g4)
    c: Horizontal(g4)
    c: Vertical(g5)
    c: Vertical(g7)
    c: Symmetric(g0,g6,g-1)
    c: Symmetric(g0,g5,g-1)
    c: Symmetric(g2,g1,g-2)
    c: Equal(g1,g5)
    c: DistanceY(g5,g0) = 3.8
    c: DistanceY(g1,g1) = 5
    c: DistanceX(g2,g2) = 10
FEATURE [PartDesign::Pocket] Pocket003
  BaseFeature = -> Pocket002
  Direction = (-1,0,0)
  Length = 7
  Length2 = 5
  Profile = -> Sketch005
  ReferenceAxis = -> Sketch005 [N_Axis]
  Refine = true
  Type = 0
FEATURE [PartDesign::Chamfer] Chamfer
  Angle = 15
  Base = -> Pocket003 [Edge30,Edge28,Edge32,Edge29,Edge31,Edge19,Edge18,Edge10,Edge14,Edge20]
  BaseFeature = -> Pocket003
  ChamferType = 0
  FlipDirection = false
  Refine = true
  Size = 0.4
  Size2 = 0.2
  SupportTransform = false
  UseAllEdges = false
FEATURE [PartDesign::Plane] DatumPlane
  Length = 60
  MapMode = 5
  Placement = pos=(-14,0,0) rot=(0.57735,-0.57735,-0.57735;2.0944rad)
  ResizeMode = 0
  Support = -> [Chamfer]
  Width = 60
FEATURE [Sketcher::SketchObject] Sketch006
  FullyConstrained = true
  MapMode = 5
  Placement = pos=(-14,0,0) rot=(0.57735,-0.57735,-0.57735;2.0944rad)
  Support = -> [DatumPlane]
  sketch-geometry (2):
    g0: Circle CenterX=0 CenterY=0 CenterZ=0 NormalX=0 NormalY=0 NormalZ=1 AngleXU=0 Radius=2.45
    g1: Circle CenterX=0 CenterY=0 CenterZ=0 NormalX=0 NormalY=0 NormalZ=1 AngleXU=0 Radius=3
  constraints (4):
    c: Coincident(g0,g-1)
    c: Coincident(g1,g0)
    c: Diameter(g0) = 4.9
    c: Diameter(g1) = 6
FEATURE [PartDesign::Pocket] Pocket004
  BaseFeature = -> Chamfer
  Direction = (1,0,0)
  Length = 5
  Length2 = 5
  Profile = -> Sketch006
  ReferenceAxis = -> Sketch006 [N_Axis]
  Refine = true
  Reversed = true
  Type = 1
FEATURE [PartDesign::Body] Body001  label="shaft1s"
  Group = -> [Sketch003,Revolution001,Sketch004,Pocket002,Sketch005,Pocket003,Chamfer,DatumPlane,Sketch006,Pocket004]
  Origin = -> Origin002
  Tip = -> Pocket004
FEATURE [App::Part] Part  label="shaft1"
  Group = -> [Body,Body001]
  Origin = -> Origin
PROVENANCE & LICENSES
A FreeCAD (.FCStd) document from a public repository crawl; recipes are the document's own serialized feature recipes (and, for linked parts, companion documents' recipes).
License: lgpl-3.0.
